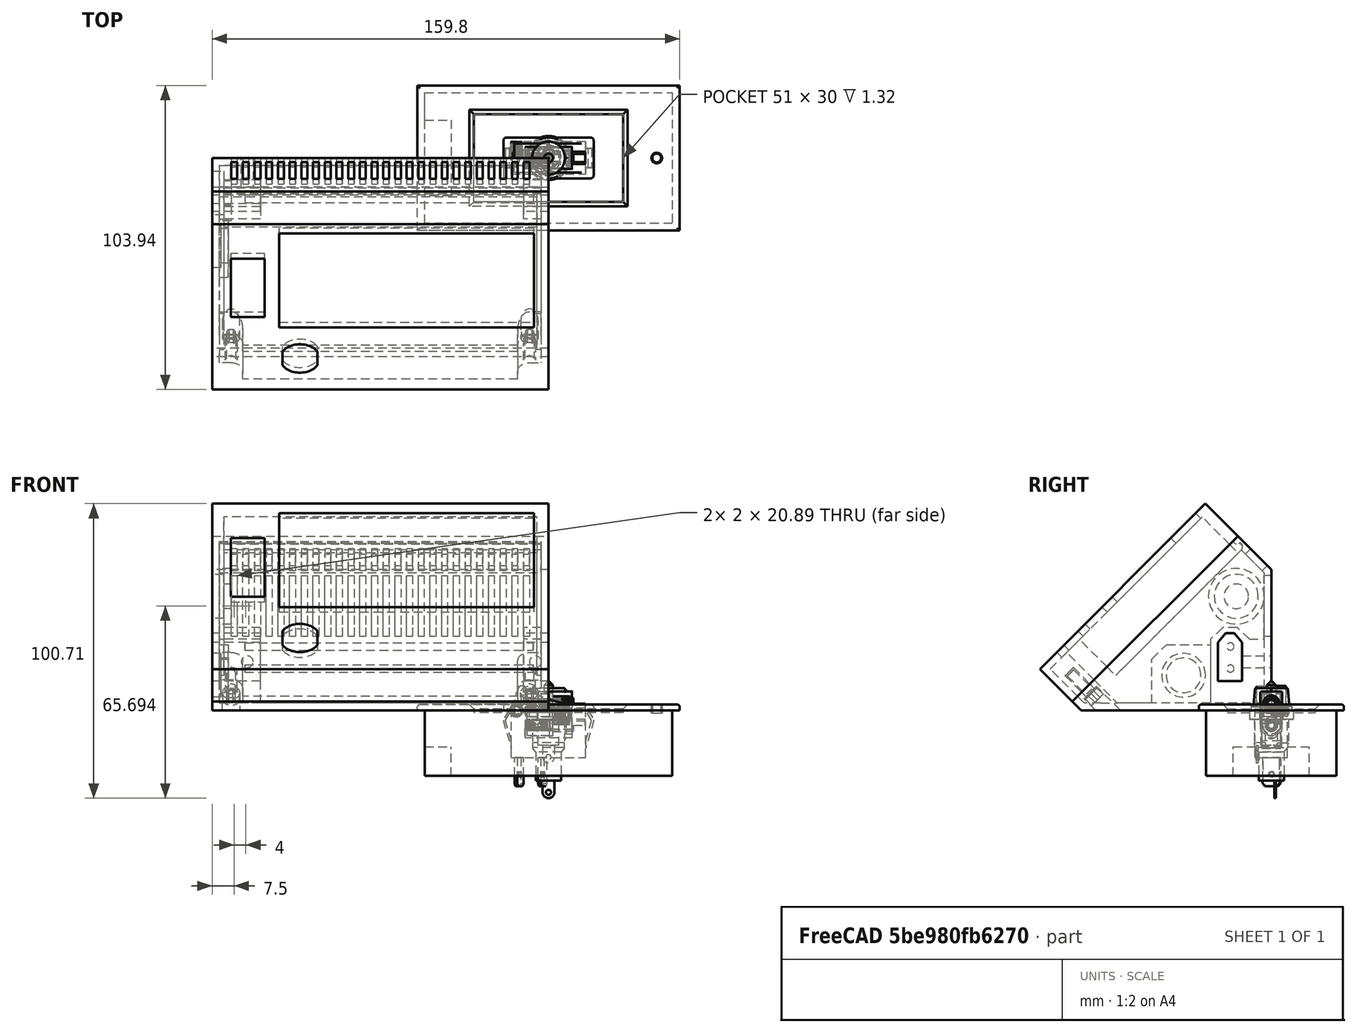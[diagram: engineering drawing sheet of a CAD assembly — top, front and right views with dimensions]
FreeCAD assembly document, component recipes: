
FREECAD ASSEMBLY — COMPONENT RECIPES ("moduleUI_017_Sur_base35mm_007.5")

This assembly document has 18 components, labeled P0..P17 below (a component is one placed body or linked part). 11 of them carry a construction recipe — the FreeCAD feature program that regenerates the part from scratch, quoted from this document or its linked companion documents; the rest are supplied as boundary geometry only. No exploded tour is included for this assembly.
COMPONENT P0 — recipe-attached ("base", modeled in this document).
Construction recipe (the document's own serialized feature program — sketch geometry with constraints, then the solid features built on it; lengths are millimeters unless a unit is written):

FEATURE [PartDesign::FeatureBase] Clone
  BaseFeature = -> Slice_child0
FEATURE [PartDesign::Thickness] Thickness
  Base = -> Clone [Face7]
  BaseFeature = -> Clone
  Intersection = false
  Join = 0
  Mode = 0
  Reversed = true
  SupportTransform = false
  Value = 2.5
  expr: Value = <<sp>>.epaisseurParois
FEATURE [PartDesign::Plane] DatumPlane001  label="planXt"
  AttachmentOffset = pos=(0,0,-2.5) rot=(0,0,1;0rad)
  Length = 110.737
  MapMode = 5
  Placement = pos=(-2.5,6e-16,-6e-16) rot=(0.57735,0.57735,0.57735;2.0944rad)
  ResizeMode = 0
  Support = -> [YZ_Plane002]
  Width = 102.305
  expr: .AttachmentOffset.Base.z = -<<sp>>.epaisseurParois
FEATURE [Sketcher::SketchObject] Sketch002  label="sk_renfortXt"
  FullyConstrained = true
  MapMode = 5
  Placement = pos=(-2.5,6e-16,-6e-16) rot=(0.57735,0.57735,0.57735;2.0944rad)
  Support = -> [DatumPlane001]
  expr: .Constraints.dist = <<sp>>.xt60distanceAngleBord
  expr: .Constraints.epRf = <<sp>>.xt60epRenfort
  expr: Constraints[13] = <<sp>>.xt60largeurFetiere
  expr: Constraints[14] = <<sp>>.xt60hauteur
  expr: Constraints[15] = <<sp>>.xt60hauteurToit
  expr: Constraints[16] = <<sp>>.xt60base
  expr: Constraints[18] = .Constraints.dist
  expr: Constraints[31] = <<sp>>.epaisseurParois
  expr: Constraints[32] = .Constraints.epRf
  expr: Constraints[34] = .Constraints.epRf
  expr: Constraints[45] = <<sp>>.epaisseurParois
  sketch-geometry (17):
    g0: LineSegment StartX=-18.3 StartY=10 StartZ=0 EndX=-18.3 EndY=23.25 EndZ=0
    g1: LineSegment StartX=-18.3 StartY=23.25 StartZ=0 EndX=-15.65 EndY=25.75 EndZ=0
    g2: LineSegment StartX=-15.65 StartY=25.75 StartZ=0 EndX=-12.65 EndY=25.75 EndZ=0
    g3: LineSegment StartX=-12.65 StartY=25.75 StartZ=0 EndX=-10 EndY=23.25 EndZ=0
    g4: LineSegment StartX=-10 StartY=23.25 StartZ=0 EndX=-10 EndY=10 EndZ=0
    g5: LineSegment StartX=-10 StartY=10 StartZ=0 EndX=-18.3 EndY=10 EndZ=0
    g6: LineSegment StartX=-14.15 StartY=10 StartZ=0 EndX=-14.15 EndY=25.75 EndZ=0
    g7: LineSegment StartX=-16.6431 StartY=28.25 StartZ=0 EndX=-20.8 EndY=24.3284 EndZ=0
    g8: LineSegment StartX=-20.8 StartY=24.3284 StartZ=0 EndX=-20.8 EndY=2.5 EndZ=0
    g9: LineSegment StartX=-20.8 StartY=2.5 StartZ=0 EndX=-7.5 EndY=2.5 EndZ=0
    g10: LineSegment StartX=-7.5 StartY=2.5 StartZ=0 EndX=-7.5 EndY=24.3284 EndZ=0
    g11: LineSegment StartX=-7.5 StartY=24.3284 StartZ=0 EndX=-11.6569 EndY=28.25 EndZ=0
    g12: LineSegment StartX=-11.6569 StartY=28.25 StartZ=0 EndX=-16.6431 EndY=28.25 EndZ=0
    g13: LineSegment StartX=-7.5 StartY=24.3284 StartZ=0 EndX=-2.5 EndY=24.3284 EndZ=0
    g14: LineSegment StartX=-2.5 StartY=24.3284 StartZ=0 EndX=-2.5 EndY=2.5 EndZ=0
    g15: LineSegment StartX=-2.5 StartY=2.5 StartZ=0 EndX=-7.5 EndY=2.5 EndZ=0
    g16: LineSegment StartX=-7.5 StartY=2.5 StartZ=0 EndX=-7.5 EndY=24.3284 EndZ=0
  constraints (46):
    c: Vertical(g0)
    c: Coincident(g0,g1)
    c: Coincident(g1,g2)
    c: Horizontal(g2)
    c: Coincident(g2,g3)
    c: Coincident(g3,g4)
    c: Vertical(g4)
    c: Coincident(g4,g5)
    c: Coincident(g5,g0)
    c: Horizontal(g5)
    c: Symmetric(g1,g2,g6)
    c: Equal(g0,g4)
    c: Symmetric(g0,g4,g6)
    c: DistanceX(g2,g2) = 3
    c: DistanceY(g4,g4) = 13.25
    c: DistanceY(g3,g2) = 2.5
    c: DistanceX(g5,g5) = 8.3
    c: DistanceX(g4,g-1) = 10  'dist'
    c: DistanceY(g-1,g4) = 10
    c: Coincident(g7,g8)
    c: Vertical(g8)
    c: Coincident(g8,g9)
    c: Horizontal(g9)
    c: Coincident(g9,g10)
    c: Coincident(g10,g11)
    c: Coincident(g11,g12)
    c: Coincident(g12,g7)
    c: Symmetric(g7,g10,g6)
    c: Symmetric(g7,g11,g6)
    c: Symmetric(g8,g9,g6)
    c: DistanceX(g8,g0) = 2.5  'epRf'
    c: DistanceY(g-1,g9) = 2.5
    c: Distance(g7,g1) = 2.5
    c: Parallel(g1,g7)
    c: DistanceY(g2,g11) = 2.5
    c: Coincident(g13,g14)
    c: Coincident(g14,g15)
    c: Coincident(g15,g16)
    c: Coincident(g16,g13)
    c: Horizontal(g13)
    c: Horizontal(g15)
    c: Vertical(g14)
    c: Vertical(g16)
    c: Coincident(g13,g11)
    c: Horizontal(g14,g9)
    c: DistanceX(g14,g-1) = 2.5
FEATURE [PartDesign::Pad] Pad001  label="renfortXt"
  AllowMultiFace = false
  BaseFeature = -> Thickness
  Direction = (1,-1e-16,1e-16)
  Length = 110
  Length2 = 100
  Profile = -> Sketch002
  Reversed = true
  Type = 0
  expr: Length = <<sp>>.largeurModuleBase - 2 * <<sp>>.epaisseurParois
FEATURE [Sketcher::SketchObject] Sketch003  label="sk_trouXt"
  FullyConstrained = true
  MapMode = 5
  Placement = pos=(0,0,0) rot=(0.57735,0.57735,0.57735;2.0944rad)
  Support = -> [YZ_Plane002]
  expr: .Constraints.dist = <<sp>>.xt60distanceAngleBord
  expr: Constraints[13] = <<sp>>.xt60base
  expr: Constraints[14] = <<sp>>.xt60hauteur
  expr: Constraints[15] = <<sp>>.xt60hauteurToit + <<sp>>.xtJeu
  expr: Constraints[16] = <<sp>>.xt60largeurFetiere
  expr: Constraints[18] = .Constraints.dist
  sketch-geometry (7):
    g0: LineSegment StartX=-18.3 StartY=10 StartZ=0 EndX=-18.3 EndY=23.25 EndZ=0
    g1: LineSegment StartX=-18.3 StartY=23.25 StartZ=0 EndX=-15.65 EndY=26.35 EndZ=0
    g2: LineSegment StartX=-15.65 StartY=26.35 StartZ=0 EndX=-12.65 EndY=26.35 EndZ=0
    g3: LineSegment StartX=-12.65 StartY=26.35 StartZ=0 EndX=-10 EndY=23.25 EndZ=0
    g4: LineSegment StartX=-10 StartY=23.25 StartZ=0 EndX=-10 EndY=10 EndZ=0
    g5: LineSegment StartX=-10 StartY=10 StartZ=0 EndX=-18.3 EndY=10 EndZ=0
    g6: LineSegment StartX=-14.15 StartY=10 StartZ=0 EndX=-14.15 EndY=26.35 EndZ=0
  constraints (19):
    c: Vertical(g0)
    c: Coincident(g0,g1)
    c: Coincident(g1,g2)
    c: Horizontal(g2)
    c: Coincident(g2,g3)
    c: Coincident(g3,g4)
    c: Coincident(g4,g5)
    c: Coincident(g5,g0)
    c: Horizontal(g5)
    c: Symmetric(g1,g2,g6)
    c: Symmetric(g0,g3,g6)
    c: Vertical(g6)
    c: Symmetric(g0,g4,g6)
    c: DistanceX(g5,g5) = 8.3
    c: DistanceY(g4,g4) = 13.25
    c: DistanceY(g3,g2) = 3.1
    c: DistanceX(g2,g2) = 3
    c: DistanceX(g4,g-1) = 10  'dist'
    c: DistanceY(g-1,g4) = 10
FEATURE [PartDesign::Pocket] Pocket
  AllowMultiFace = false
  BaseFeature = -> Pad001
  Direction = (-1,2e-16,-3e-16)
  Length = 115
  Length2 = 100
  Profile = -> Sketch003
  Type = 0
  expr: Length = <<sp>>.largeurModuleBase
FEATURE [PartDesign::Plane] DatumPlane002  label="planDecoupeRenfortXt"
  AttachmentOffset = pos=(0,0,2.5) rot=(0,0,1;0rad)
  Length = 161.762
  MapMode = 5
  Placement = pos=(0,-2.5,-6e-16) rot=(1,0,0;1.5708rad)
  ResizeMode = 0
  Support = -> [XZ_Plane002]
  Width = 106.331
  expr: .AttachmentOffset.Base.z = <<sp>>.epaisseurParois
FEATURE [Sketcher::SketchObject] Sketch004  label="sk_decoupRenfXt"
  FullyConstrained = true
  MapMode = 5
  Placement = pos=(0,-2.5,-6e-16) rot=(1,0,0;1.5708rad)
  Support = -> [DatumPlane002]
  expr: Constraints[10] = <<sp>>.xt60LongueurRenfortPetit + <<sp>>.epaisseurParois
  expr: Constraints[11] = <<sp>>.largeurModuleBase - (<<sp>>.xt60longueurRenfortGrand + <<sp>>.epaisseurParois)
  expr: Constraints[8] = <<sp>>.epaisseurParois
  expr: Constraints[9] = <<sp>>.xt60distanceAngleBord + <<sp>>.xt60hauteur + <<sp>>.xt60hauteurToit + <<sp>>.xt60epRenfort
  sketch-geometry (4):
    g0: LineSegment StartX=-98.5 StartY=28.25 StartZ=0 EndX=-8.5 EndY=28.25 EndZ=0
    g1: LineSegment StartX=-8.5 StartY=28.25 StartZ=0 EndX=-8.5 EndY=2.5 EndZ=0
    g2: LineSegment StartX=-8.5 StartY=2.5 StartZ=0 EndX=-98.5 EndY=2.5 EndZ=0
    g3: LineSegment StartX=-98.5 StartY=2.5 StartZ=0 EndX=-98.5 EndY=28.25 EndZ=0
  constraints (12):
    c: Coincident(g0,g1)
    c: Coincident(g1,g2)
    c: Coincident(g2,g3)
    c: Coincident(g3,g0)
    c: Horizontal(g0)
    c: Horizontal(g2)
    c: Vertical(g1)
    c: Vertical(g3)
    c: DistanceY(g-1,g1) = 2.5
    c: DistanceY(g-1,g0) = 28.25
    c: DistanceX(g1,g-1) = 8.5
    c: DistanceX(g2,g-1) = 98.5
FEATURE [PartDesign::Pocket] Pocket001  label="decoupeRenfXt"
  AllowMultiFace = false
  BaseFeature = -> Pocket
  Direction = (0,1,2e-16)
  Length = 23.3
  Length2 = 100
  Profile = -> Sketch004
  Reversed = true
  Type = 0
  expr: Length = <<sp>>.xt60distanceAngleBord + <<sp>>.xt60base + 2 * <<sp>>.xt60epRenfort
FEATURE [Sketcher::SketchObject] Sketch005  label="xt60PercagePostMale"
  FullyConstrained = true
  MapMode = 5
  Placement = pos=(0,0,0) rot=(1,0,0;1.5708rad)
  Support = -> [XZ_Plane002]
  expr: Constraints[0] = <<sp>>.insertDiamPercage
  expr: Constraints[1] = <<sp>>.insertDistanceTrouBordMale
  expr: Constraints[2] = <<sp>>.insertHauteur
  sketch-geometry (1):
    g0: Circle CenterX=-4.5 CenterY=16.625 CenterZ=0 NormalX=0 NormalY=0 NormalZ=1 AngleXU=0 Radius=2
  constraints (3):
    c: Diameter(g0) = 4
    c: DistanceX(g0,g-1) = 4.5
    c: DistanceY(g-1,g0) = 16.625
FEATURE [PartDesign::Pocket] Pocket002  label="insertXtMale"
  AllowMultiFace = false
  BaseFeature = -> Pocket001
  Direction = (0,1,2e-16)
  Length = 10
  Length2 = 100
  Profile = -> Sketch005
  Reversed = true
  Type = 0
  expr: Length = <<sp>>.insertProfondeurPercage
FEATURE [Sketcher::SketchObject] Sketch006  label="xt60PercagePostFem"
  FullyConstrained = true
  MapMode = 5
  Placement = pos=(0,0,0) rot=(1,0,0;1.5708rad)
  Support = -> [XZ_Plane002]
  expr: Constraints[0] = <<sp>>.insertDiamPercage
  expr: Constraints[1] = <<sp>>.insertDistanceTrouBordFem
  expr: Constraints[2] = <<sp>>.insertHauteur
  sketch-geometry (1):
    g0: Circle CenterX=-103 CenterY=16.625 CenterZ=0 NormalX=0 NormalY=0 NormalZ=1 AngleXU=0 Radius=2
  constraints (3):
    c: Diameter(g0) = 4
    c: DistanceX(g0,g-1) = 103
    c: DistanceY(g-1,g0) = 16.625
FEATURE [PartDesign::Pocket] Pocket003  label="insertXt60Fem"
  AllowMultiFace = false
  BaseFeature = -> Pocket002
  Direction = (0,1,2e-16)
  Length = 10
  Length2 = 100
  Profile = -> Sketch006
  Reversed = true
  Type = 0
  expr: Length = <<sp>>.insertProfondeurPercage
FEATURE [PartDesign::Plane] DatumPlane003
  AttachmentOffset = pos=(0,0,2.5) rot=(0,0,1;0rad)
  Length = 162.821
  MapMode = 2
  Placement = pos=(0,0,2.5) rot=(0,0,1;0rad)
  ResizeMode = 0
  Support = -> [XY_Plane002]
  Width = 115.821
  expr: .AttachmentOffset.Base.z = <<sp>>.epaisseurParois
FEATURE [PartDesign::Plane] DatumPlane004  label="planTrancheur"
  AttachmentOffset = pos=(0,0,71) rot=(-1,0,0;0.785398rad)
  Length = 166.517
  MapMode = 5
  Placement = pos=(0,-71,-1.58e-14) rot=(1,0,0;0.785398rad)
  ResizeMode = 0
  Support = -> [XZ_Plane002]
  Width = 152.077
  expr: .AttachmentOffset.Base.z = <<sp>>.planTrancheur
FEATURE [Sketcher::SketchObject] Sketch008
  FullyConstrained = true
  MapMode = 5
  Placement = pos=(0,-71,-2.13e-14) rot=(1,0,0;0.785398rad)
  Support = -> [DatumPlane004]
  expr: .Constraints.dist = <<sp>>.epaisseurParois
  expr: Constraints[13] = <<sp>>.epaisseurParois
  expr: Constraints[16] = <<sp>>.insertDiamPercage / 2 + <<sp>>.insertFAVMargeDist
  expr: Constraints[1] = <<sp>>.insertFavDistAuZeroDuPLan
  expr: Constraints[21] = <<sp>>.insertFAVDistBord
  expr: Constraints[22] = <<sp>>.largeurModuleBase - <<sp>>.epaisseurParois
  sketch-geometry (7):
    g0: LineSegment StartX=-2.5 StartY=4.24264 StartZ=0 EndX=-112.5 EndY=4.24264 EndZ=0
    g1: LineSegment StartX=-6.5 StartY=14.7426 StartZ=0 EndX=-2.5 EndY=14.7426 EndZ=0
    g2: LineSegment StartX=-2.5 StartY=14.7426 StartZ=0 EndX=-2.5 EndY=6.74264 EndZ=0
    g3: LineSegment StartX=-2.5 StartY=6.74264 StartZ=0 EndX=-10.5 EndY=6.74264 EndZ=0
    g4: LineSegment StartX=-10.5 StartY=6.74264 StartZ=0 EndX=-10.5 EndY=10.7426 EndZ=0
    g5: ArcOfCircle CenterX=-6.5 CenterY=10.7426 CenterZ=0 NormalX=0 NormalY=0 NormalZ=1 AngleXU=0 Radius=4 StartAngle=1.5708 EndAngle=3.14159
    g6: LineSegment StartX=-6.5 StartY=10.7426 StartZ=0 EndX=-6.5 EndY=6.74264 EndZ=0
  constraints (23):
    c: Horizontal(g0)
    c: DistanceY(g-1,g0) = 4.24264
    c: DistanceX(g0,g-1) = 2.5  'dist'
    c: Horizontal(g1)
    c: Coincident(g1,g2)
    c: Vertical(g2)
    c: Coincident(g2,g3)
    c: Horizontal(g3)
    c: Coincident(g3,g4)
    c: Vertical(g4)
    c: Vertical(g2,g0)
    c: Equal(g3,g2)
    c: Equal(g4,g1)
    c: DistanceY(g0,g2) = 2.5
    c: Coincident(g5,g4)
    c: Coincident(g5,g1)
    c: DistanceX(g5,g2) = 4
    c: Coincident(g6,g5)
    c: PointOnObject(g6,g3)
    c: Vertical(g6)
    c: Vertical(g5,g1)
    c: DistanceX(g3,g3) = 8
    c: DistanceX(g0,g-1) = 112.5
FEATURE [PartDesign::Pad] Pad003  label="padTrouFAVDroite"
  AllowMultiFace = false
  BaseFeature = -> Pocket003
  Direction = (0,-0.707107,0.707107)
  Length = 10
  Length2 = 100
  Profile = -> Sketch008
  Reversed = true
  Type = 3
  UpToFace = -> DatumPlane003
FEATURE [Sketcher::SketchObject] Sketch009
  FullyConstrained = true
  MapMode = 5
  Placement = pos=(0,-71,-2.13e-14) rot=(1,0,0;0.785398rad)
  Support = -> [DatumPlane004]
  expr: .Constraints.larg = <<sp>>.insertFAVDistBord
  expr: Constraints[11] = .Constraints.larg / 2
  expr: Constraints[12] = <<sp>>.largeurModuleBase
  expr: Constraints[13] = <<sp>>.insertFavDistAuZeroDuPLan
  expr: Constraints[14] = <<sp>>.epaisseurParois
  expr: Constraints[15] = <<sp>>.epaisseurParois
  expr: Constraints[8] = .Constraints.larg
  sketch-geometry (6):
    g0: LineSegment StartX=-112.5 StartY=6.74264 StartZ=0 EndX=-104.5 EndY=6.74264 EndZ=0
    g1: LineSegment StartX=-104.5 StartY=6.74264 StartZ=0 EndX=-104.5 EndY=10.7426 EndZ=0
    g2: LineSegment StartX=-108.5 StartY=14.7426 StartZ=0 EndX=-112.5 EndY=14.7426 EndZ=0
    g3: LineSegment StartX=-112.5 StartY=14.7426 StartZ=0 EndX=-112.5 EndY=6.74264 EndZ=0
    g4: ArcOfCircle CenterX=-108.5 CenterY=10.7426 CenterZ=0 NormalX=0 NormalY=0 NormalZ=1 AngleXU=0 Radius=4 StartAngle=0 EndAngle=1.5708
    g5: GeomPoint X=-115 Y=4.24264 Z=0
  constraints (16):
    c: Coincident(g0,g1)
    c: Coincident(g2,g3)
    c: Coincident(g3,g0)
    c: Horizontal(g0)
    c: Horizontal(g2)
    c: Vertical(g1)
    c: Vertical(g3)
    c: DistanceX(g0,g0) = 8  'larg'
    c: DistanceY(g3,g3) = 8
    c: Tangent(g2,g4) = -1.5708
    c: Tangent(g1,g4) = -1.5708
    c: DistanceX(g0,g4) = 4
    c: DistanceX(g5,g-1) = 115
    c: DistanceY(g-1,g5) = 4.24264
    c: DistanceX(g5,g0) = 2.5
    c: DistanceY(g5,g0) = 2.5
FEATURE [PartDesign::Pad] Pad004  label="padTrouFavGauche"
  AllowMultiFace = false
  BaseFeature = -> Pad003
  Direction = (0,-0.707107,0.707107)
  Length = 10
  Length2 = 100
  Profile = -> Sketch009
  Type = 3
  UpToFace = -> DatumPlane003 [Plane]
FEATURE [Sketcher::SketchObject] Sketch010
  FullyConstrained = true
  MapMode = 5
  Placement = pos=(0,-71,-2.13e-14) rot=(1,0,0;0.785398rad)
  Support = -> [DatumPlane004]
  expr: Constraints[0] = <<sp>>.insertFAVDistBord / 2 + <<sp>>.epaisseurParois
  expr: Constraints[1] = <<sp>>.insertFavDistAuZeroDuPLan + <<sp>>.epaisseurParois + <<sp>>.insertFAVDistBord / 2
  expr: Constraints[2] = <<sp>>.insertDiamPercage
  sketch-geometry (1):
    g0: Circle CenterX=-6.5 CenterY=10.7426 CenterZ=0 NormalX=0 NormalY=0 NormalZ=1 AngleXU=0 Radius=2
  constraints (3):
    c: DistanceX(g0,g-1) = 6.5
    c: DistanceY(g-1,g0) = 10.7426
    c: Diameter(g0) = 4
FEATURE [PartDesign::Pocket] Pocket004  label="trouDroit"
  AllowMultiFace = false
  BaseFeature = -> Pad004
  Direction = (0,0.707107,-0.707107)
  Length = 5
  Length2 = 100
  Profile = -> Sketch010
  Type = 1
FEATURE [Sketcher::SketchObject] Sketch011
  FullyConstrained = true
  MapMode = 5
  Placement = pos=(0,-71,-2.13e-14) rot=(1,0,0;0.785398rad)
  Support = -> [DatumPlane004]
  expr: Constraints[0] = <<sp>>.insertDiamPercage
  expr: Constraints[1] = <<sp>>.largeurModuleBase - <<sp>>.epaisseurParois - <<sp>>.insertFAVDistBord / 2
  expr: Constraints[2] = <<sp>>.insertFavDistAuZeroDuPLan + <<sp>>.epaisseurParois + <<sp>>.insertFAVDistBord / 2
  sketch-geometry (1):
    g0: Circle CenterX=-108.5 CenterY=10.7426 CenterZ=0 NormalX=0 NormalY=0 NormalZ=1 AngleXU=0 Radius=2
  constraints (3):
    c: Diameter(g0) = 4
    c: DistanceX(g0,g-1) = 108.5
    c: DistanceY(g-1,g0) = 10.7426
FEATURE [PartDesign::Pocket] Pocket005  label="trouGauche"
  AllowMultiFace = false
  BaseFeature = -> Pocket004
  Direction = (0,0.707107,-0.707107)
  Length = 5
  Length2 = 100
  Profile = -> Sketch011
  Type = 1
FEATURE [PartDesign::Plane] DatumPlane005  label="planTeteVisFav"
  AttachmentOffset = pos=(0,0,68) rot=(-1,0,0;0.785398rad)
  Length = 166.517
  MapMode = 5
  Placement = pos=(0,-68,-1.51e-14) rot=(1,0,0;0.785398rad)
  ResizeMode = 0
  Support = -> [XZ_Plane002]
  Width = 152.077
  expr: .AttachmentOffset.Base.z = <<sp>>.planTrancheur - 3
FEATURE [Sketcher::SketchObject] Sketch012
  ExternalGeometry = -> [Pocket005]
  FullyConstrained = true
  MapMode = 5
  Placement = pos=(0,-68,-1.42e-14) rot=(1,0,0;0.785398rad)
  Support = -> [DatumPlane005]
  expr: Constraints[1] = <<sp>>.visM3DiamEncastrement
  sketch-geometry (2):
    g0: Circle CenterX=-6.5 CenterY=8.62132 CenterZ=0 NormalX=0 NormalY=0 NormalZ=1 AngleXU=0 Radius=3
    g1: Circle CenterX=-108.5 CenterY=8.62132 CenterZ=0 NormalX=0 NormalY=0 NormalZ=1 AngleXU=0 Radius=3
  constraints (4):
    c: Equal(g0,g1)
    c: Diameter(g1) = 6
    c: Coincident(g1,g-4)
    c: Coincident(g-3,g0)
FEATURE [PartDesign::Pocket] Pocket006  label="evidementTeteVisFav"
  AllowMultiFace = false
  BaseFeature = -> Pocket005
  Direction = (0,0.707107,-0.707107)
  Length = 20
  Length2 = 100
  Profile = -> Sketch012
  Type = 1
FEATURE [Sketcher::SketchObject] Sketch014
  FullyConstrained = true
  MapMode = 5
  Placement = pos=(0,0,0) rot=(1,0,0;1.5708rad)
  Support = -> [XZ_Plane002]
  expr: Constraints[12] = <<sp>>.xt60distanceAngleBord + <<sp>>.xt60hauteur + <<sp>>.ventilDistBordFente
  expr: Constraints[13] = <<sp>>.ventilLargeurFentes
  expr: Constraints[14] = <<sp>>.ventilEcartfente / 2
  expr: Constraints[15] = <<sp>>.hauteurDuDos - <<sp>>.ventilDistBordFente
  expr: Constraints[2] = <<sp>>.hauteurDuDos
  expr: Constraints[3] = <<sp>>.largeurModuleBase / 2
  sketch-geometry (5):
    g0: LineSegment StartX=-57.5 StartY=0 StartZ=0 EndX=-57.5 EndY=48.1371 EndZ=0
    g1: LineSegment StartX=-60.5 StartY=46.1371 StartZ=0 EndX=-58.5 EndY=46.1371 EndZ=0
    g2: LineSegment StartX=-58.5 StartY=46.1371 StartZ=0 EndX=-58.5 EndY=25.25 EndZ=0
    g3: LineSegment StartX=-58.5 StartY=25.25 StartZ=0 EndX=-60.5 EndY=25.25 EndZ=0
    g4: LineSegment StartX=-60.5 StartY=25.25 StartZ=0 EndX=-60.5 EndY=46.1371 EndZ=0
  constraints (16):
    c: PointOnObject(g0,g-1)
    c: Vertical(g0)
    c: DistanceY(g0,g0) = 48.1371
    c: DistanceX(g0,g-1) = 57.5
    c: Coincident(g1,g2)
    c: Coincident(g2,g3)
    c: Coincident(g3,g4)
    c: Coincident(g4,g1)
    c: Horizontal(g1)
    c: Horizontal(g3)
    c: Vertical(g2)
    c: Vertical(g4)
    c: DistanceY(g-1,g2) = 25.25
    c: DistanceX(g1,g1) = 2
    c: DistanceX(g2,g0) = 1
    c: DistanceY(g-1,g1) = 46.1371
FEATURE [PartDesign::Pocket] Pocket008  label="ventilFente1"
  AllowMultiFace = false
  BaseFeature = -> Pocket006
  Direction = (0,1,2e-16)
  Length = 2.5
  Length2 = 100
  Profile = -> Sketch014
  Reversed = true
  Type = 0
  expr: Length = <<sp>>.epaisseurParois
FEATURE [PartDesign::LinearPattern] LinearPattern  label="ventilDosRepeat1"
  BaseFeature = -> Pocket008
  Direction = -> Sketch014 [H_Axis]
  Length = 48
  Occurrences = 13
  Originals = -> [Pocket008]
  Reversed = true
  expr: Length = <<sp>>.ventilLargeurRepet
  expr: Occurrences = <<sp>>.ventilNbrFents
FEATURE [PartDesign::LinearPattern] LinearPattern001  label="ventilDosRepeat2"
  BaseFeature = -> LinearPattern
  Direction = -> Sketch014 [H_Axis]
  Length = 52
  Occurrences = 14
  Originals = -> [Pocket008]
  expr: Length = <<sp>>.ventilLargeurRepet + <<sp>>.ventilEcartfente + <<sp>>.ventilLargeurFentes
  expr: Occurrences = <<sp>>.ventilNbrFents + 1
FEATURE [PartDesign::Plane] DatumPlane006  label="planVentilSup"
  AttachmentOffset = pos=(0,0,-48.1371) rot=(1,0,0;0.785398rad)
  Length = 166.517
  MapMode = 5
  Placement = pos=(0,48.1371,1.07e-14) rot=(1,0,0;2.35619rad)
  ResizeMode = 0
  Support = -> [XZ_Plane002]
  Width = 152.077
  expr: .AttachmentOffset.Base.z = -<<sp>>.hauteurDuDos
FEATURE [Sketcher::SketchObject] Sketch015
  FullyConstrained = true
  MapMode = 5
  Placement = pos=(0,48.1371,1.07e-14) rot=(1,0,0;2.35619rad)
  Support = -> [DatumPlane006]
  expr: Constraints[10] = <<sp>>.ventilLargeurFentes
  expr: Constraints[11] = (<<sp>>.largeurModuleBase + <<sp>>.ventilEcartfente) / 2
  expr: Constraints[8] = <<sp>>.distanceAuZeroPlanBorArriere + <<sp>>.ventilDistBordFente
  expr: Constraints[9] = <<sp>>.longPetitRetSupSansFav - 2 * <<sp>>.ventilDistBordFente - <<sp>>.favBordureProf
  sketch-geometry (4):
    g0: LineSegment StartX=-58.5 StartY=78.0926 StartZ=0 EndX=-60.5 EndY=78.0926 EndZ=0
    g1: LineSegment StartX=-60.5 StartY=78.0926 StartZ=0 EndX=-60.5 EndY=70.0761 EndZ=0
    g2: LineSegment StartX=-60.5 StartY=70.0761 StartZ=0 EndX=-58.5 EndY=70.0761 EndZ=0
    g3: LineSegment StartX=-58.5 StartY=70.0761 StartZ=0 EndX=-58.5 EndY=78.0926 EndZ=0
  constraints (12):
    c: Coincident(g0,g1)
    c: Coincident(g1,g2)
    c: Coincident(g2,g3)
    c: Coincident(g3,g0)
    c: Horizontal(g0)
    c: Horizontal(g2)
    c: Vertical(g1)
    c: Vertical(g3)
    c: DistanceY(g-1,g2) = 70.0761
    c: DistanceY(g2,g0) = 8.01652
    c: DistanceX(g0,g0) = 2
    c: DistanceX(g2,g-1) = 58.5
FEATURE [PartDesign::Pocket] Pocket009  label="ventilSupFente"
  AllowMultiFace = false
  BaseFeature = -> LinearPattern001
  Direction = (0,0.707107,0.707107)
  Length = 5
  Length2 = 100
  Profile = -> Sketch015
  Reversed = true
  Type = 0
FEATURE [PartDesign::LinearPattern] LinearPattern002  label="ventilSupRepeat1"
  BaseFeature = -> Pocket009
  Direction = -> Sketch015 [H_Axis]
  Length = 48
  Occurrences = 13
  Originals = -> [Pocket009]
  Reversed = true
  expr: Length = <<sp>>.ventilLargeurRepet
  expr: Occurrences = <<sp>>.ventilNbrFents
FEATURE [PartDesign::LinearPattern] LinearPattern003  label="ventilSupRepeat2"
  BaseFeature = -> LinearPattern002
  Direction = -> Sketch015 [H_Axis]
  Length = 52
  Occurrences = 14
  Originals = -> [Pocket009]
  expr: Length = <<sp>>.ventilLargeurRepet + <<sp>>.ventilEcartfente + <<sp>>.ventilLargeurFentes
  expr: Occurrences = <<sp>>.ventilNbrFents + 1
FEATURE [PartDesign::Body] Body001  label="base"
  BaseFeature = -> Slice_child0
  Group = -> [Clone,Thickness,DatumPlane001,Sketch002,Pad001,Sketch003,Pocket,DatumPlane002,Sketch004,Pocket001,Sketch005,Pocket002,Sketch006,Pocket003,DatumPlane003,DatumPlane004,Sketch008,Pad003,Sketch009,Pad004,Sketch010,Pocket004,Sketch011,Pocket005,DatumPlane005,Sketch012,Pocket006,Sketch014,Pocket008,LinearPattern,LinearPattern001,DatumPlane006,Sketch015,Pocket009,LinearPattern002,LinearPattern003,+15 more]
  Origin = -> Origin002
  Tip = -> Pocket029
COMPONENT P1 — recipe-attached ("faceAvant", modeled in this document).
Construction recipe (the document's own serialized feature program — sketch geometry with constraints, then the solid features built on it; lengths are millimeters unless a unit is written):

FEATURE [PartDesign::FeatureBase] Clone001
  BaseFeature = -> Slice_child1
FEATURE [PartDesign::Thickness] Thickness001
  Base = -> Clone001 [Face5]
  BaseFeature = -> Clone001
  Intersection = false
  Join = 0
  Mode = 0
  Reversed = true
  SupportTransform = false
  Value = 2.5
  expr: Value = <<sp>>.epaisseurParois
FEATURE [PartDesign::Plane] DatumPlane007  label="planTrancheurBis"
  AttachmentOffset = pos=(0,0,71) rot=(-1,0,0;0.785398rad)
  Length = 168.131
  MapMode = 5
  Placement = pos=(0,-71,-1.58e-14) rot=(1,0,0;0.785398rad)
  ResizeMode = 0
  Support = -> [XZ_Plane003]
  Width = 169.449
  expr: .AttachmentOffset.Base.z = <<sp>>.planTrancheur
FEATURE [Sketcher::SketchObject] Sketch016  label="sk_insertFavDroit"
  FullyConstrained = true
  MapMode = 5
  Placement = pos=(0,-71,-2.13e-14) rot=(1,0,0;0.785398rad)
  Support = -> [DatumPlane007]
  expr: Constraints[11] = <<sp>>.insertFAVDistBord
  expr: Constraints[14] = <<sp>>.insertFAVDistBord / 2
  expr: Constraints[7] = <<sp>>.epaisseurParois
  expr: Constraints[8] = <<sp>>.insertFavDistAuZeroDuPLan + <<sp>>.epaisseurParois
  expr: Constraints[9] = <<sp>>.insertFAVDistBord
  sketch-geometry (5):
    g0: LineSegment StartX=-6.5 StartY=14.7426 StartZ=0 EndX=-2.5 EndY=14.7426 EndZ=0
    g1: LineSegment StartX=-2.5 StartY=14.7426 StartZ=0 EndX=-2.5 EndY=6.74264 EndZ=0
    g2: LineSegment StartX=-2.5 StartY=6.74264 StartZ=0 EndX=-10.5 EndY=6.74264 EndZ=0
    g3: LineSegment StartX=-10.5 StartY=6.74264 StartZ=0 EndX=-10.5 EndY=10.7426 EndZ=0
    g4: ArcOfCircle CenterX=-6.5 CenterY=10.7426 CenterZ=0 NormalX=0 NormalY=0 NormalZ=1 AngleXU=0 Radius=4 StartAngle=1.5708 EndAngle=3.14159
  constraints (15):
    c: Horizontal(g0)
    c: Coincident(g0,g1)
    c: Vertical(g1)
    c: Coincident(g1,g2)
    c: Horizontal(g2)
    c: Coincident(g2,g3)
    c: Vertical(g3)
    c: DistanceX(g1,g-1) = 2.5
    c: DistanceY(g-1,g1) = 6.74264
    c: DistanceY(g1,g1) = 8
    c: Equal(g3,g0)
    c: DistanceX(g2,g2) = 8
    c: Coincident(g4,g0)
    c: Tangent(g4,g3) = 1.5708
    c: DistanceX(g4,g1) = 4
FEATURE [PartDesign::Pad] Pad005  label="padInsertFavDroit"
  AllowMultiFace = false
  BaseFeature = -> Thickness001
  Direction = (1,1,1)
  Length = 10
  Length2 = 100
  Profile = -> Sketch016
  Type = 2
FEATURE [Sketcher::SketchObject] Sketch017  label="sp_padInserFavGauch"
  FullyConstrained = true
  MapMode = 5
  Placement = pos=(0,-71,-2.13e-14) rot=(1,0,0;0.785398rad)
  Support = -> [DatumPlane007]
  expr: Constraints[10] = <<sp>>.insertFAVDistBord
  expr: Constraints[12] = <<sp>>.insertFAVDistBord / 2
  expr: Constraints[13] = <<sp>>.largeurModuleBase
  expr: Constraints[14] = <<sp>>.insertFavDistAuZeroDuPLan
  expr: Constraints[15] = <<sp>>.epaisseurParois
  expr: Constraints[16] = <<sp>>.epaisseurParois
  sketch-geometry (6):
    g0: LineSegment StartX=-108.5 StartY=14.7426 StartZ=0 EndX=-112.5 EndY=14.7426 EndZ=0
    g1: LineSegment StartX=-112.5 StartY=14.7426 StartZ=0 EndX=-112.5 EndY=6.74264 EndZ=0
    g2: LineSegment StartX=-112.5 StartY=6.74264 StartZ=0 EndX=-104.5 EndY=6.74264 EndZ=0
    g3: LineSegment StartX=-104.5 StartY=6.74264 StartZ=0 EndX=-104.5 EndY=10.7426 EndZ=0
    g4: ArcOfCircle CenterX=-108.5 CenterY=10.7426 CenterZ=0 NormalX=0 NormalY=0 NormalZ=1 AngleXU=0 Radius=4 StartAngle=2.3e-15 EndAngle=1.5708
    g5: GeomPoint X=-115 Y=4.24264 Z=0
  constraints (17):
    c: Horizontal(g0)
    c: Coincident(g0,g1)
    c: Vertical(g1)
    c: Coincident(g1,g2)
    c: Horizontal(g2)
    c: Coincident(g2,g3)
    c: Vertical(g3)
    c: Equal(g3,g0)
    c: Equal(g2,g1)
    c: Coincident(g0,g4)
    c: DistanceX(g2,g2) = 8
    c: Tangent(g4,g3) = -1.5708
    c: DistanceX(g0,g0) = 4
    c: DistanceX(g5,g-1) = 115
    c: DistanceY(g-1,g5) = 4.24264
    c: DistanceY(g5,g1) = 2.5
    c: DistanceX(g5,g1) = 2.5
FEATURE [PartDesign::Pad] Pad006  label="padInsertFavGauch"
  AllowMultiFace = false
  BaseFeature = -> Pad005
  Direction = (1,1,1)
  Length = 10
  Length2 = 100
  Profile = -> Sketch017
  Type = 2
FEATURE [Sketcher::SketchObject] Sketch018  label="skPercageInsertFavDroit"
  FullyConstrained = true
  MapMode = 5
  Placement = pos=(0,-71,-2.13e-14) rot=(1,0,0;0.785398rad)
  Support = -> [DatumPlane007]
  expr: Constraints[0] = <<sp>>.insertDiamPercage
  expr: Constraints[1] = <<sp>>.insertFavDistAuZeroDuPLan + <<sp>>.epaisseurParois + <<sp>>.insertFAVDistBord / 2
  expr: Constraints[2] = <<sp>>.epaisseurParois + <<sp>>.insertFAVDistBord / 2
  expr: Constraints[7] = <<sp>>.largeurModuleBase - 2 * <<sp>>.epaisseurParois - <<sp>>.insertFAVDistBord
  sketch-geometry (3):
    g0: Circle CenterX=-6.5 CenterY=10.7426 CenterZ=0 NormalX=0 NormalY=0 NormalZ=1 AngleXU=0 Radius=2
    g1: Circle CenterX=-108.5 CenterY=10.7426 CenterZ=0 NormalX=0 NormalY=0 NormalZ=1 AngleXU=0 Radius=2
    g2: LineSegment StartX=-108.5 StartY=10.7426 StartZ=0 EndX=-6.5 EndY=10.7426 EndZ=0
  constraints (8):
    c: Diameter(g0) = 4
    c: DistanceY(g-1,g0) = 10.7426
    c: DistanceX(g0,g-1) = 6.5
    c: Equal(g0,g1)
    c: Coincident(g2,g1)
    c: Coincident(g2,g0)
    c: Horizontal(g2)
    c: DistanceX(g2,g2) = 102
FEATURE [PartDesign::Pocket] Pocket010  label="trouInsertFavDroit"
  AllowMultiFace = false
  BaseFeature = -> Pad006
  Direction = (1,1,1)
  Length = 8
  Length2 = 100
  Profile = -> Sketch018
  Reversed = true
  Type = 0
  expr: Length = <<sp>>.insertFavProfondeur
FEATURE [PartDesign::Plane] DatumPlane011  label="planFaceAvant"
  AttachmentOffset = pos=(0,0,93.2843) rot=(-1,0,0;0.785398rad)
  Length = 168.131
  MapMode = 5
  Placement = pos=(0,-93.2843,-2.07e-14) rot=(1,0,0;0.785398rad)
  ResizeMode = 0
  Support = -> [XZ_Plane003]
  Width = 169.449
  expr: .AttachmentOffset.Base.z = <<sp>>.planFaceAvant
FEATURE [Sketcher::SketchObject] Sketch030  label="sk_rebordFav"
  FullyConstrained = true
  MapMode = 5
  Placement = pos=(0,-71,-2.13e-14) rot=(1,0,0;0.785398rad)
  Support = -> [DatumPlane007]
  expr: Constraints[0] = <<sp>>.insertFavDistAuZeroDuPLan
  expr: Constraints[19] = <<sp>>.epaisseurParois
  expr: Constraints[20] = <<sp>>.favEpBordure
  expr: Constraints[21] = <<sp>>.favDistBordPlan
  expr: Constraints[22] = <<sp>>.largeurModuleBase - 2 * <<sp>>.epaisseurParois
  expr: Constraints[23] = <<sp>>.favEpBordure
  expr: Constraints[24] = <<sp>>.Face - <<sp>>.epaisseurParois
  expr: Constraints[25] = <<sp>>.favEpBordure
  sketch-geometry (9):
    g0: GeomPoint X=0 Y=4.24264 Z=0
    g1: LineSegment StartX=-112.5 StartY=20.9853 StartZ=0 EndX=-112.5 EndY=81.7426 EndZ=0
    g2: LineSegment StartX=-112.5 StartY=81.7426 StartZ=0 EndX=-2.5 EndY=81.7426 EndZ=0
    g3: LineSegment StartX=-2.5 StartY=81.7426 StartZ=0 EndX=-2.5 EndY=20.9853 EndZ=0
    g4: LineSegment StartX=-2.5 StartY=20.9853 StartZ=0 EndX=-4 EndY=20.9853 EndZ=0
    g5: LineSegment StartX=-4 StartY=20.9853 StartZ=0 EndX=-4 EndY=80.2426 EndZ=0
    g6: LineSegment StartX=-4 StartY=80.2426 StartZ=0 EndX=-111 EndY=80.2426 EndZ=0
    g7: LineSegment StartX=-111 StartY=80.2426 StartZ=0 EndX=-111 EndY=20.9853 EndZ=0
    g8: LineSegment StartX=-111 StartY=20.9853 StartZ=0 EndX=-112.5 EndY=20.9853 EndZ=0
  constraints (26):
    c: DistanceY(g-1,g0) = 4.24264
    c: Vertical(g0,g-1)
    c: Vertical(g1)
    c: Coincident(g1,g2)
    c: Horizontal(g2)
    c: Coincident(g2,g3)
    c: Vertical(g3)
    c: Coincident(g3,g4)
    c: Horizontal(g4)
    c: Coincident(g4,g5)
    c: Vertical(g5)
    c: Coincident(g5,g6)
    c: Horizontal(g6)
    c: Coincident(g6,g7)
    c: Vertical(g7)
    c: Coincident(g7,g8)
    c: Coincident(g8,g1)
    c: Horizontal(g8)
    c: Horizontal(g7,g4)
    c: DistanceX(g3,g0) = 2.5
    c: DistanceX(g4,g4) = 1.5
    c: DistanceY(g0,g3) = 16.7426
    c: DistanceX(g1,g3) = 110
    c: DistanceY(g5,g2) = 1.5
    c: DistanceY(g0,g2) = 77.5
    c: DistanceX(g1,g7) = 1.5
FEATURE [PartDesign::Pad] Pad014  label="favRebordSupport"
  AllowMultiFace = false
  BaseFeature = -> Pocket010
  Direction = (1,1,1)
  Length = 10
  Length2 = 100
  Profile = -> Sketch030
  Type = 3
  UpToFace = -> Pocket010 [Face13]
FEATURE [PartDesign::Pad] Pad015  label="favRebord"
  AllowMultiFace = false
  BaseFeature = -> Pad014
  Direction = (1,1,1)
  Length = 4.15
  Length2 = 100
  Profile = -> Sketch030
  Reversed = true
  Type = 0
  expr: Length = <<sp>>.favBordureProf
FEATURE [Sketcher::SketchObject] Sketch031  label="sk_bourlet"
  ExternalGeometry = -> [Pad015]
  FullyConstrained = true
  MapMode = 5
  Placement = pos=(-2.5,0,0) rot=(0.57735,0.57735,0.57735;2.0944rad)
  Support = -> [Pad015]
  expr: Constraints[3] = <<sp>>.bourletMaintientRayon - <<sp>>.bourletRayonJeu
  sketch-geometry (2):
    g0: ArcOfCircle CenterX=-11.184 CenterY=55.7855 CenterZ=0 NormalX=0 NormalY=0 NormalZ=1 AngleXU=0 Radius=1.3 StartAngle=5.49779 EndAngle=8.63938
    g1: LineSegment StartX=-12.1032 StartY=56.7048 StartZ=0 EndX=-10.2647 EndY=54.8663 EndZ=0
  constraints (6):
    c: Coincident(g0,g-3)
    c: PointOnObject(g0,g-3)
    c: PointOnObject(g0,g-3)
    c: Radius(g0) = 1.3
    c: Coincident(g1,g0)
    c: Coincident(g1,g0)
FEATURE [PartDesign::Pad] Pad016  label="bourlet"
  AllowMultiFace = false
  BaseFeature = -> Pad015
  Direction = (1,1,1)
  Length = 10
  Length2 = 100
  Profile = -> Sketch031
  Reversed = true
  Type = 3
  UpToFace = -> Pad015 [Face11]
FEATURE [Sketcher::SketchObject] Sketch040  label="sk_trouFav"
  FullyConstrained = true
  MapMode = 5
  Placement = pos=(0,-93.2843,-2.84e-14) rot=(1,0,0;0.785398rad)
  Support = -> [DatumPlane011]
  expr: Constraints[16] = <<sp>>.distZeroPlanFAV
  expr: Constraints[18] = <<SW_C1500AT>>.trouLargeur
  expr: Constraints[19] = <<SW_C1500AT>>.trouLongeur
  expr: Constraints[20] = <<favPos>>.SwitchPosX
  expr: Constraints[21] = <<favPos>>.switchPosY
  expr: Constraints[22] = <<KTD132>>.trouLongeur + <<KTD132>>.trouJeuLong
  expr: Constraints[23] = <<KTD132>>.trouLargeur + <<KTD132>>.trouJeuLarg
  expr: Constraints[24] = <<favPos>>.ecranPosX
  expr: Constraints[25] = <<favPos>>.ecranPosY
  expr: Constraints[26] = <<favPos>>.FusePosX
  expr: Constraints[27] = <<favPos>>.FusePosY
  expr: Constraints[28] = <<fuse>>.corpsPercageDiam + <<fuse>>.corpsPercageJeu
  expr: Constraints[40] = <<fuse>>.corpsLargeurMeplat + <<fuse>>.corpsPercageJeu
  sketch-geometry (14):
    g0: LineSegment StartX=-92.1 StartY=95.4 StartZ=0 EndX=-5 EndY=95.4 EndZ=0
    g1: LineSegment StartX=-5 StartY=95.4 StartZ=0 EndX=-5 EndY=50 EndZ=0
    g2: LineSegment StartX=-5 StartY=50 StartZ=0 EndX=-92.1 EndY=50 EndZ=0
    g3: LineSegment StartX=-92.1 StartY=50 StartZ=0 EndX=-92.1 EndY=95.4 EndZ=0
    g4: LineSegment StartX=-108.55 StartY=83.25 StartZ=0 EndX=-97 EndY=83.25 EndZ=0
    g5: LineSegment StartX=-97 StartY=83.25 StartZ=0 EndX=-97 EndY=55 EndZ=0
    g6: LineSegment StartX=-97 StartY=55 StartZ=0 EndX=-108.55 EndY=55 EndZ=0
    g7: LineSegment StartX=-108.55 StartY=55 StartZ=0 EndX=-108.55 EndY=83.25 EndZ=0
    g8: ArcOfCircle CenterX=-85 CenterY=35 CenterZ=0 NormalX=0 NormalY=0 NormalZ=1 AngleXU=0 Radius=6.85 StartAngle=3.65999 EndAngle=5.76479
    g9: GeomPoint X=0 Y=20 Z=0
    g10: LineSegment StartX=-90.95 StartY=38.3941 StartZ=0 EndX=-90.95 EndY=31.6059 EndZ=0
    g11: LineSegment StartX=-79.05 StartY=31.6059 StartZ=0 EndX=-79.05 EndY=38.3941 EndZ=0
    g12: LineSegment StartX=-90.95 StartY=38.3941 StartZ=0 EndX=-79.05 EndY=38.3941 EndZ=0
    g13: ArcOfCircle CenterX=-85 CenterY=35 CenterZ=0 NormalX=0 NormalY=0 NormalZ=1 AngleXU=0 Radius=6.85 StartAngle=0.5184 EndAngle=2.62319
  constraints (41):
    c: Coincident(g0,g1)
    c: Coincident(g1,g2)
    c: Coincident(g2,g3)
    c: Coincident(g3,g0)
    c: Horizontal(g0)
    c: Horizontal(g2)
    c: Vertical(g1)
    c: Vertical(g3)
    c: Coincident(g4,g5)
    c: Coincident(g5,g6)
    c: Coincident(g6,g7)
    c: Coincident(g7,g4)
    c: Horizontal(g4)
    c: Horizontal(g6)
    c: Vertical(g5)
    c: Vertical(g7)
    c: DistanceY(g-1,g9) = 20
    c: Vertical(g-1,g9)
    c: DistanceX(g4,g4) = 11.55
    c: DistanceY(g7,g7) = 28.25
    c: DistanceX(g5,g9) = 97
    c: DistanceY(g9,g5) = 35
    c: DistanceX(g0,g0) = 87.1
    c: DistanceY(g1,g1) = 45.4
    c: DistanceX(g1,g9) = 5
    c: DistanceY(g9,g1) = 30
    c: DistanceX(g8,g9) = 85
    c: DistanceY(g9,g8) = 15
    c: Diameter(g8) = 13.7
    c: Vertical(g10)
    c: Vertical(g11)
    c: Coincident(g12,g10)
    c: Coincident(g12,g11)
    c: Horizontal(g12)
    c: Coincident(g8,g10)
    c: Coincident(g13,g10)
    c: Equal(g8,g13)
    c: Coincident(g8,g11)
    c: Coincident(g13,g11)
    c: Coincident(g8,g13)
    c: DistanceX(g12,g12) = 11.9
FEATURE [PartDesign::Pocket] Pocket022  label="favPercee"
  BaseFeature = -> Pad016
  Direction = (1,1,1)
  Length = 5
  Length2 = 100
  Profile = -> Sketch040
  Type = 1
FEATURE [PartDesign::Body] Body002  label="faceAvant"
  BaseFeature = -> Slice_child1
  Group = -> [Clone001,Thickness001,DatumPlane007,Sketch016,Pad005,Sketch017,Pad006,Sketch018,Pocket010,DatumPlane011,Sketch030,Pad014,Pad015,Sketch031,Pad016,Sketch040,Pocket022]
  Origin = -> Origin003
  Tip = -> Pocket022
COMPONENT P2 — recipe-attached ("visTHCM3x10_001", modeled in this document).
Construction recipe (the document's own serialized feature program — sketch geometry with constraints, then the solid features built on it; lengths are millimeters unless a unit is written):

FEATURE [Sketcher::SketchObject] Sketch020
  FullyConstrained = false
  MapMode = 5
  Support = -> [XY_Plane006]
  sketch-geometry (1):
    g0: Circle CenterX=0 CenterY=0 CenterZ=0 NormalX=0 NormalY=0 NormalZ=1 AngleXU=0 Radius=2.75
  constraints (2):
    c: Coincident(g0,g-1)
    c: Diameter(g0) = 5.5
FEATURE [PartDesign::Pad] Pad008  label="tete"
  AllowMultiFace = false
  Direction = (1,1,1)
  Length = 3
  Length2 = 100
  Profile = -> Sketch020
  Type = 0
FEATURE [Sketcher::SketchObject] Sketch001
  FullyConstrained = false
  MapMode = 5
  Placement = pos=(0,0,0) rot=(1,0,0;3.14159rad)
  Support = -> [Pad008]
  sketch-geometry (1):
    g0: Circle CenterX=0 CenterY=0 CenterZ=0 NormalX=0 NormalY=0 NormalZ=1 AngleXU=0 Radius=1.5
  constraints (2):
    c: Coincident(g0,g-1)
    c: Diameter(g0) = 3
FEATURE [PartDesign::Pad] Pad009  label="corps"
  AllowMultiFace = false
  BaseFeature = -> Pad008
  Direction = (1,1,1)
  Length = 10
  Length2 = 100
  Profile = -> Sketch001
  Type = 0
FEATURE [PartDesign::Plane] DatumPlane008
  AttachmentOffset = pos=(0,0,3) rot=(0,0,1;0rad)
  Length = 60
  MapMode = 5
  Placement = pos=(0,0,3) rot=(0,0,1;0rad)
  ResizeMode = 0
  Support = -> [XY_Plane006]
  Width = 60
FEATURE [Sketcher::SketchObject] Sketch021
  FullyConstrained = false
  MapMode = 5
  Placement = pos=(0,0,3) rot=(0,0,1;0rad)
  Support = -> [DatumPlane008]
  sketch-geometry (7):
    g0: LineSegment StartX=0.721688 StartY=-1.25 StartZ=0 EndX=1.44338 EndY=1.0119e-12 EndZ=0
    g1: LineSegment StartX=1.44338 StartY=1.0119e-12 StartZ=0 EndX=0.721688 EndY=1.25 EndZ=0
    g2: LineSegment StartX=0.721688 StartY=1.25 StartZ=0 EndX=-0.721688 EndY=1.25 EndZ=0
    g3: LineSegment StartX=-0.721688 StartY=1.25 StartZ=0 EndX=-1.44338 EndY=8.689e-13 EndZ=0
    g4: LineSegment StartX=-1.44338 StartY=8.689e-13 StartZ=0 EndX=-0.721688 EndY=-1.25 EndZ=0
    g5: LineSegment StartX=-0.721688 StartY=-1.25 StartZ=0 EndX=0.721688 EndY=-1.25 EndZ=0
    g6: Circle CenterX=0 CenterY=0 CenterZ=0 NormalX=0 NormalY=0 NormalZ=1 AngleXU=0 Radius=1.44338
  constraints (16):
    c: Coincident(g0,g1)
    c: Coincident(g1,g2)
    c: Coincident(g2,g3)
    c: Coincident(g3,g4)
    c: Coincident(g4,g5)
    c: Coincident(g5,g0)
    c: Equal(g0, g1-g5) x5
    c: PointOnObject(g0,g6)
    c: PointOnObject(g1,g6)
    c: PointOnObject(g2,g6)
    c: PointOnObject(g3,g6)
    c: PointOnObject(g4,g6)
    c: PointOnObject(g5,g6)
    c: Coincident(g6,g-1)
    c: Horizontal(g2)
    c: DistanceY(g0,g1) = 2.5
FEATURE [PartDesign::Pocket] Pocket011  label="emprunte"
  AllowMultiFace = false
  BaseFeature = -> Pad009
  Direction = (1,1,1)
  Length = 4
  Length2 = 100
  Profile = -> Sketch021
  Type = 0
FEATURE [PartDesign::Body] Body003  label="visTHCM3x10_001"
  Group = -> [Sketch020,Pad008,Sketch001,Pad009,DatumPlane008,Sketch021,Pocket011]
  Origin = -> Origin010
  Placement = pos=(-6.5,-61.582,5.72756) rot=(1,0,0;3.92699rad)
  Tip = -> Pocket011
COMPONENT P3 — recipe-attached ("visTHCM3x10_002", modeled in this document).
Construction recipe (the document's own serialized feature program — sketch geometry with constraints, then the solid features built on it; lengths are millimeters unless a unit is written):

FEATURE [PartDesign::Plane] DatumPlane009
  AttachmentOffset = pos=(0,0,3) rot=(0,0,1;0rad)
  Length = 60
  MapMode = 5
  Placement = pos=(0,0,3) rot=(0,0,1;0rad)
  ResizeMode = 0
  Support = -> [XY_Plane007]
  Width = 60
FEATURE [Sketcher::SketchObject] Sketch022
  FullyConstrained = false
  MapMode = 5
  Support = -> [XY_Plane007]
  sketch-geometry (1):
    g0: Circle CenterX=0 CenterY=0 CenterZ=0 NormalX=0 NormalY=0 NormalZ=1 AngleXU=0 Radius=2.75
  constraints (2):
    c: Coincident(g0,g-1)
    c: Diameter(g0) = 5.5
FEATURE [PartDesign::Pad] Pad011  label="tete001"
  AllowMultiFace = false
  Direction = (1,1,1)
  Length = 3
  Length2 = 100
  Profile = -> Sketch022
  Type = 0
FEATURE [Sketcher::SketchObject] Sketch023
  FullyConstrained = false
  MapMode = 5
  Placement = pos=(0,0,0) rot=(1,0,0;3.14159rad)
  Support = -> [Pad011]
  sketch-geometry (1):
    g0: Circle CenterX=0 CenterY=0 CenterZ=0 NormalX=0 NormalY=0 NormalZ=1 AngleXU=0 Radius=1.5
  constraints (2):
    c: Coincident(g0,g-1)
    c: Diameter(g0) = 3
FEATURE [PartDesign::Pad] Pad010  label="corps001"
  AllowMultiFace = false
  BaseFeature = -> Pad011
  Direction = (1,1,1)
  Length = 10
  Length2 = 100
  Profile = -> Sketch023
  Type = 0
FEATURE [Sketcher::SketchObject] Sketch024
  FullyConstrained = false
  MapMode = 5
  Placement = pos=(0,0,3) rot=(0,0,1;0rad)
  Support = -> [DatumPlane009]
  sketch-geometry (7):
    g0: LineSegment StartX=0.721688 StartY=-1.25 StartZ=0 EndX=1.44338 EndY=1.0119e-12 EndZ=0
    g1: LineSegment StartX=1.44338 StartY=1.0119e-12 StartZ=0 EndX=0.721688 EndY=1.25 EndZ=0
    g2: LineSegment StartX=0.721688 StartY=1.25 StartZ=0 EndX=-0.721688 EndY=1.25 EndZ=0
    g3: LineSegment StartX=-0.721688 StartY=1.25 StartZ=0 EndX=-1.44338 EndY=8.689e-13 EndZ=0
    g4: LineSegment StartX=-1.44338 StartY=8.689e-13 StartZ=0 EndX=-0.721688 EndY=-1.25 EndZ=0
    g5: LineSegment StartX=-0.721688 StartY=-1.25 StartZ=0 EndX=0.721688 EndY=-1.25 EndZ=0
    g6: Circle CenterX=0 CenterY=0 CenterZ=0 NormalX=0 NormalY=0 NormalZ=1 AngleXU=0 Radius=1.44338
  constraints (16):
    c: Coincident(g0,g1)
    c: Coincident(g1,g2)
    c: Coincident(g2,g3)
    c: Coincident(g3,g4)
    c: Coincident(g4,g5)
    c: Coincident(g5,g0)
    c: Equal(g0, g1-g5) x5
    c: PointOnObject(g0,g6)
    c: PointOnObject(g1,g6)
    c: PointOnObject(g2,g6)
    c: PointOnObject(g3,g6)
    c: PointOnObject(g4,g6)
    c: PointOnObject(g5,g6)
    c: Coincident(g6,g-1)
    c: Horizontal(g2)
    c: DistanceY(g0,g1) = 2.5
FEATURE [PartDesign::Pocket] Pocket012  label="emprunte001"
  AllowMultiFace = false
  BaseFeature = -> Pad010
  Direction = (1,1,1)
  Length = 4
  Length2 = 100
  Profile = -> Sketch024
  Type = 0
FEATURE [PartDesign::Body] Body004  label="visTHCM3x10_002"
  Group = -> [Sketch022,Pad011,Sketch023,Pad010,DatumPlane009,Sketch024,Pocket012]
  Origin = -> Origin011
  Placement = pos=(-108.5,-61.582,5.72756) rot=(1,0,0;3.92699rad)
  Tip = -> Pocket012
COMPONENT P4 — recipe-attached ("DC5525", modeled in this document).
Construction recipe (the document's own serialized feature program — sketch geometry with constraints, then the solid features built on it; lengths are millimeters unless a unit is written):

FEATURE [Sketcher::SketchObject] Sketch  label="profileDeBase"
  FullyConstrained = true
  MapMode = 5
  Placement = pos=(0,0,0) rot=(0.57735,0.57735,0.57735;2.0944rad)
  Support = -> [YZ_Plane001]
  expr: Constraints[10] = <<sp>>.petitRetour
  expr: Constraints[11] = <<sp>>.angleFacePetitRetour
  expr: Constraints[12] = <<sp>>.Face
  expr: Constraints[13] = <<sp>>.angleFaceRetourHaut
  expr: Constraints[8] = <<sp>>.Base
  expr: Constraints[9] = <<sp>>.anglePetitRetourBase
  sketch-geometry (5):
    g0: LineSegment StartX=0 StartY=0 StartZ=0 EndX=-65 EndY=0 EndZ=0
    g1: LineSegment StartX=-65 StartY=0 StartZ=0 EndX=-79.1421 EndY=14.1421 EndZ=0
    g2: LineSegment StartX=-79.1421 StartY=14.1421 StartZ=0 EndX=-22.5736 EndY=70.7107 EndZ=0
    g3: LineSegment StartX=-22.5736 StartY=70.7107 StartZ=0 EndX=0 EndY=48.1371 EndZ=0
    g4: LineSegment StartX=0 StartY=48.1371 StartZ=0 EndX=0 EndY=0 EndZ=0
  constraints (14):
    c: Coincident(g-1,g0)
    c: Horizontal(g0)
    c: Coincident(g0,g1)
    c: Coincident(g1,g2)
    c: Coincident(g2,g3)
    c: PointOnObject(g3,g-2)
    c: Coincident(g3,g4)
    c: Coincident(g4,g0)
    c: DistanceX(g0,g0) = 65
    c: Angle(g0,g1) = 2.35619
    c: Distance(g1) = 20
    c: Angle(g1,g2) = 1.5708
    c: Distance(g2) = 80
    c: Angle(g2,g3) = 1.5708
FEATURE [PartDesign::Pad] Pad
  AllowMultiFace = false
  Direction = (1,1,1)
  Length = 115
  Length2 = 100
  Placement = pos=(0,0,0) rot=(0.57735,0.57735,0.57735;2.0944rad)
  Profile = -> Sketch
  Reversed = true
  Type = 0
  expr: Length = <<sp>>.largeurModuleBase
FEATURE [PartDesign::Plane] DatumPlane
  AttachmentOffset = pos=(71,0,0) rot=(0,-1,0;0.785398rad)
  Length = 98.6412
  MapMode = 5
  Placement = pos=(-7.9e-15,8e-15,71) rot=(0.678598,0.678598,0.281085;3.68962rad)
  ResizeMode = 0
  Support = -> [Pad]
  Width = 63.0813
FEATURE [PartDesign::Body] Body  label="Base"
  Group = -> [Sketch,Pad,DatumPlane]
  Origin = -> Origin001
  Tip = -> Pad
COMPONENT P5 — same part as P4; its construction recipe is shown at P4.
COMPONENT P6 — geometry summary ("xt60fem"; no construction recipe available for this part):
  bounding box: 20.5 x 16.5 x 7.5 mm
  tessellated surface: 23,736 triangles
  volume: 955 mm^3 (38% of its bounding box)
COMPONENT P7 — geometry summary ("xt60Male"; no construction recipe available for this part):
  bounding box: 20.2 x 16.6 x 7.5 mm
  tessellated surface: 14,992 triangles
  volume: 1201 mm^3 (48% of its bounding box)
COMPONENT P8 — geometry summary ("ZSB_RUTHEX_M3_5.7_001"; no construction recipe available for this part):
  bounding box: 5.7 x 4.6 x 4.6 mm
  tessellated surface: 4,640 triangles
  volume: 44 mm^3 (36% of its bounding box)
  symmetry: 4-fold rotationally symmetric about the y axis; mirror-symmetric across its x mid-plane, z mid-plane
COMPONENT P9 — geometry summary ("ZSB_RUTHEX_M3_5.7_002"; no construction recipe available for this part):
  bounding box: 5.7 x 4.6 x 4.6 mm
  tessellated surface: 4,640 triangles
  volume: 44 mm^3 (36% of its bounding box)
  symmetry: 4-fold rotationally symmetric about the y axis; mirror-symmetric across its x mid-plane, z mid-plane
COMPONENT P10 — geometry summary ("ZSB_RUTHEX_M3_5.7_003"; no construction recipe available for this part):
  bounding box: 6.9 x 6.9 x 4.6 mm
  tessellated surface: 4,640 triangles
  volume: 44 mm^3 (20% of its bounding box)
  symmetry: mirror-symmetric across its x mid-plane
COMPONENT P11 — geometry summary ("ZSB_RUTHEX_M3_5.7_004"; no construction recipe available for this part):
  bounding box: 6.9 x 6.9 x 4.6 mm
  tessellated surface: 4,640 triangles
  volume: 44 mm^3 (20% of its bounding box)
  symmetry: mirror-symmetric across its x mid-plane
COMPONENT P12 — recipe-attached ("partVisPointeauM3x10_001", modeled in this document).
Construction recipe (the document's own serialized feature program — sketch geometry with constraints, then the solid features built on it; lengths are millimeters unless a unit is written):

FEATURE [Sketcher::SketchObject] Sketch025
  FullyConstrained = false
  MapMode = 5
  Support = -> [XY_Plane008]
  sketch-geometry (1):
    g0: Circle CenterX=0 CenterY=0 CenterZ=0 NormalX=0 NormalY=0 NormalZ=1 AngleXU=0 Radius=1.5
  constraints (2):
    c: Coincident(g0,g-1)
    c: Diameter(g0) = 3
FEATURE [Sketcher::SketchObject] Sketch026
  FullyConstrained = false
  MapMode = 5
  Support = -> [XY_Plane008]
  sketch-geometry (7):
    g0: LineSegment StartX=0.433013 StartY=-0.75 StartZ=0 EndX=0.866025 EndY=1.25568e-11 EndZ=0
    g1: LineSegment StartX=0.866025 StartY=1.25568e-11 StartZ=0 EndX=0.433013 EndY=0.75 EndZ=0
    g2: LineSegment StartX=0.433013 StartY=0.75 StartZ=0 EndX=-0.433013 EndY=0.75 EndZ=0
    g3: LineSegment StartX=-0.433013 StartY=0.75 StartZ=0 EndX=-0.866025 EndY=2.91366e-11 EndZ=0
    g4: LineSegment StartX=-0.866025 StartY=2.91366e-11 StartZ=0 EndX=-0.433013 EndY=-0.75 EndZ=0
    g5: LineSegment StartX=-0.433013 StartY=-0.75 StartZ=0 EndX=0.433013 EndY=-0.75 EndZ=0
    g6: Circle CenterX=0 CenterY=0 CenterZ=0 NormalX=0 NormalY=0 NormalZ=1 AngleXU=0 Radius=0.866025
  constraints (16):
    c: Coincident(g0,g1)
    c: Coincident(g1,g2)
    c: Coincident(g2,g3)
    c: Coincident(g3,g4)
    c: Coincident(g4,g5)
    c: Coincident(g5,g0)
    c: Equal(g0, g1-g5) x5
    c: PointOnObject(g0,g6)
    c: PointOnObject(g1,g6)
    c: PointOnObject(g2,g6)
    c: PointOnObject(g3,g6)
    c: PointOnObject(g4,g6)
    c: PointOnObject(g5,g6)
    c: Coincident(g6,g-1)
    c: Horizontal(g2)
    c: DistanceY(g0,g1) = 1.5
FEATURE [PartDesign::Pad] Pad012
  AllowMultiFace = false
  Direction = (1,1,1)
  Length = 10
  Length2 = 100
  Profile = -> Sketch025
  Type = 0
FEATURE [PartDesign::Chamfer] Chamfer
  Angle = 45
  Base = -> Pad012 [Edge3]
  BaseFeature = -> Pad012
  ChamferType = 0
  FlipDirection = false
  Size = 1.4
  Size2 = 1
  SupportTransform = false
  UseAllEdges = false
FEATURE [PartDesign::Pocket] Pocket013
  AllowMultiFace = false
  BaseFeature = -> Chamfer
  Direction = (1,1,1)
  Length = 1.5
  Length2 = 100
  Profile = -> Sketch026
  Reversed = true
  Type = 0
FEATURE [PartDesign::Chamfer] Chamfer001
  Angle = 45
  Base = -> Pocket013 [Edge3]
  BaseFeature = -> Pocket013
  ChamferType = 0
  FlipDirection = false
  Size = 0.1
  Size2 = 1
  SupportTransform = false
  UseAllEdges = false
FEATURE [PartDesign::Body] Body005  label="bodyVisPointeauM3x10_001"
  Group = -> [Sketch025,Pad012,Chamfer,Sketch026,Pocket013,Chamfer001]
  Origin = -> Origin013
  Tip = -> Chamfer001
COMPONENT P13 — recipe-attached ("partVisPointeauM3x10_002", modeled in this document).
Construction recipe (the document's own serialized feature program — sketch geometry with constraints, then the solid features built on it; lengths are millimeters unless a unit is written):

FEATURE [Sketcher::SketchObject] Sketch027
  FullyConstrained = false
  MapMode = 5
  Support = -> [XY_Plane010]
  sketch-geometry (7):
    g0: LineSegment StartX=0.433013 StartY=-0.75 StartZ=0 EndX=0.866025 EndY=1.25568e-11 EndZ=0
    g1: LineSegment StartX=0.866025 StartY=1.25568e-11 StartZ=0 EndX=0.433013 EndY=0.75 EndZ=0
    g2: LineSegment StartX=0.433013 StartY=0.75 StartZ=0 EndX=-0.433013 EndY=0.75 EndZ=0
    g3: LineSegment StartX=-0.433013 StartY=0.75 StartZ=0 EndX=-0.866025 EndY=2.91366e-11 EndZ=0
    g4: LineSegment StartX=-0.866025 StartY=2.91366e-11 StartZ=0 EndX=-0.433013 EndY=-0.75 EndZ=0
    g5: LineSegment StartX=-0.433013 StartY=-0.75 StartZ=0 EndX=0.433013 EndY=-0.75 EndZ=0
    g6: Circle CenterX=0 CenterY=0 CenterZ=0 NormalX=0 NormalY=0 NormalZ=1 AngleXU=0 Radius=0.866025
  constraints (16):
    c: Coincident(g0,g1)
    c: Coincident(g1,g2)
    c: Coincident(g2,g3)
    c: Coincident(g3,g4)
    c: Coincident(g4,g5)
    c: Coincident(g5,g0)
    c: Equal(g0, g1-g5) x5
    c: PointOnObject(g0,g6)
    c: PointOnObject(g1,g6)
    c: PointOnObject(g2,g6)
    c: PointOnObject(g3,g6)
    c: PointOnObject(g4,g6)
    c: PointOnObject(g5,g6)
    c: Coincident(g6,g-1)
    c: Horizontal(g2)
    c: DistanceY(g0,g1) = 1.5
FEATURE [Sketcher::SketchObject] Sketch028
  FullyConstrained = false
  MapMode = 5
  Support = -> [XY_Plane010]
  sketch-geometry (1):
    g0: Circle CenterX=0 CenterY=0 CenterZ=0 NormalX=0 NormalY=0 NormalZ=1 AngleXU=0 Radius=1.5
  constraints (2):
    c: Coincident(g0,g-1)
    c: Diameter(g0) = 3
FEATURE [PartDesign::Pad] Pad013
  AllowMultiFace = false
  Direction = (1,1,1)
  Length = 10
  Length2 = 100
  Profile = -> Sketch028
  Type = 0
FEATURE [PartDesign::Chamfer] Chamfer003
  Angle = 45
  Base = -> Pad013 [Edge3]
  BaseFeature = -> Pad013
  ChamferType = 0
  FlipDirection = false
  Size = 1.4
  Size2 = 1
  SupportTransform = false
  UseAllEdges = false
FEATURE [PartDesign::Pocket] Pocket014
  AllowMultiFace = false
  BaseFeature = -> Chamfer003
  Direction = (1,1,1)
  Length = 1.5
  Length2 = 100
  Profile = -> Sketch027
  Reversed = true
  Type = 0
FEATURE [PartDesign::Chamfer] Chamfer002
  Angle = 45
  Base = -> Pocket014 [Edge3]
  BaseFeature = -> Pocket014
  ChamferType = 0
  FlipDirection = false
  Size = 0.1
  Size2 = 1
  SupportTransform = false
  UseAllEdges = false
FEATURE [PartDesign::Body] Body006  label="bodyVisPointeauM3x10_002"
  Group = -> [Sketch028,Pad013,Chamfer003,Sketch027,Pocket014,Chamfer002]
  Origin = -> Origin015
  Tip = -> Chamfer002
COMPONENT P14 — recipe-attached ("tigeLaiton001", modeled in this document).
Construction recipe (the document's own serialized feature program — sketch geometry with constraints, then the solid features built on it; lengths are millimeters unless a unit is written):

FEATURE [PartDesign::Plane] DatumPlane012  label="planBaseTige"
  AttachmentOffset = pos=(0,0,-5.18) rot=(0,0,1;0rad)
  Length = 60
  MapMode = 5
  Placement = pos=(-5.18,1.2e-15,-1.2e-15) rot=(0.57735,0.57735,0.57735;2.0944rad)
  ResizeMode = 0
  Support = -> [YZ_Plane012]
  Width = 60
  expr: .AttachmentOffset.Base.z = -<<tige>>.planBaseTigeposX
FEATURE [Sketcher::SketchObject] Sketch032  label="sk_tiges"
  FullyConstrained = true
  MapMode = 5
  Placement = pos=(-5.18,1.2e-15,-1.2e-15) rot=(0.57735,0.57735,0.57735;2.0944rad)
  Support = -> [DatumPlane012]
  expr: Constraints[0] = <<tige>>.tigeDiam
  expr: Constraints[1] = <<tige>>.tigePosY
  expr: Constraints[2] = <<tige>>.tigePosX
  sketch-geometry (1):
    g0: Circle CenterX=-14 CenterY=14.3 CenterZ=0 NormalX=0 NormalY=0 NormalZ=1 AngleXU=0 Radius=1.25
  constraints (3):
    c: Diameter(g0) = 2.5
    c: DistanceY(g-1,g0) = 14.3
    c: DistanceX(g0,g-1) = 14
FEATURE [PartDesign::Pad] Pad017  label="tigeBasse"
  AllowMultiFace = false
  Direction = (1,1,1)
  Length = 98.62
  Length2 = 100
  Placement = pos=(-5.18,1e-15,-1e-15) rot=(0.57735,0.57735,0.57735;2.0944rad)
  Profile = -> Sketch032
  Reversed = true
  Type = 0
  expr: Length = <<tige>>.tigeLong
FEATURE [PartDesign::Body] Body007  label="tigeLaiton"
  Group = -> [DatumPlane012,Sketch032,Pad017]
  Origin = -> Origin016
  Tip = -> Pad017
FEATURE [PartDesign::Plane] DatumPlane013  label="planTige2"
  AttachmentOffset = pos=(0,0,-5.18) rot=(0,0,1;0rad)
  Length = 60
  MapMode = 5
  Placement = pos=(-5.18,1.2e-15,-1.2e-15) rot=(0.57735,0.57735,0.57735;2.0944rad)
  ResizeMode = 0
  Support = -> [YZ_Plane014]
  Width = 60
  expr: .AttachmentOffset.Base.z = -<<tige>>.planBaseTigeposX
FEATURE [Sketcher::SketchObject] Sketch033  label="sk_tige2"
  FullyConstrained = true
  MapMode = 5
  Placement = pos=(-5.18,1.2e-15,-1.2e-15) rot=(0.57735,0.57735,0.57735;2.0944rad)
  Support = -> [DatumPlane013]
  expr: Constraints[0] = <<tige>>.tigeDiam
  expr: Constraints[1] = <<tige>>.tigePosX
  expr: Constraints[2] = <<tige>>.tigePosY + <<tige>>.xtEcartBroches
  sketch-geometry (1):
    g0: Circle CenterX=-14 CenterY=21.86 CenterZ=0 NormalX=0 NormalY=0 NormalZ=1 AngleXU=0 Radius=1.25
  constraints (3):
    c: Diameter(g0) = 2.5
    c: DistanceX(g0,g-1) = 14
    c: DistanceY(g-1,g0) = 21.86
FEATURE [PartDesign::Pad] Pad018
  AllowMultiFace = false
  Direction = (1,1,1)
  Length = 98.62
  Length2 = 100
  Placement = pos=(-5.18,1e-15,-1e-15) rot=(0.57735,0.57735,0.57735;2.0944rad)
  Profile = -> Sketch033
  Reversed = true
  Type = 0
  expr: Length = <<tige>>.tigeLong
FEATURE [PartDesign::Body] Body008  label="tige2"
  Group = -> [DatumPlane013,Sketch033,Pad018]
  Origin = -> Origin018
  Tip = -> Pad018
COMPONENT P15 — recipe-attached ("porteFuse", modeled in this document).
Construction recipe (the document's own serialized feature program — sketch geometry with constraints, then the solid features built on it; lengths are millimeters unless a unit is written):

FEATURE [Sketcher::SketchObject] Sketch041
  FullyConstrained = false
  MapMode = 5
  Placement = pos=(0,0,0) rot=(1,0,0;1.5708rad)
  Support = -> [XZ_Plane042]
  expr: Constraints[20] = <<fuse>>.corpsDiamExt / 2
  expr: Constraints[22] = <<fuse>>.corpsHautTot
  expr: Constraints[23] = <<fuse>>.CorpsLongFutInferier
  expr: Constraints[24] = <<fuse>>.corpsDiamFutInferieur / 2
  expr: Constraints[26] = <<fuse>>.corpsDiamFilletage / 2
  expr: Constraints[27] = <<fuse>>.corpsLevreHauteur
  expr: Constraints[28] = <<fuse>>.corpsHauteurFilletage
  sketch-geometry (11):
    g0: LineSegment StartX=3.565 StartY=-12 StartZ=0 EndX=3.565 EndY=0 EndZ=0
    g1: LineSegment StartX=3.565 StartY=0 StartZ=0 EndX=7.5 EndY=0 EndZ=0
    g2: LineSegment StartX=7.5 StartY=0 StartZ=0 EndX=7.5 EndY=-3 EndZ=0
    g3: LineSegment StartX=7.5 StartY=-3 StartZ=0 EndX=5.85 EndY=-3 EndZ=0
    g4: LineSegment StartX=5.85 StartY=-3 StartZ=0 EndX=5.85 EndY=-11 EndZ=0
    g5: LineSegment StartX=5.85 StartY=-11 StartZ=0 EndX=5.5925 EndY=-12.7105 EndZ=0
    g6: LineSegment StartX=5.5925 StartY=-12.7105 StartZ=0 EndX=4.335 EndY=-14.2 EndZ=0
    g7: LineSegment StartX=4.335 StartY=-14.2 StartZ=0 EndX=4.335 EndY=-24 EndZ=0
    g8: LineSegment StartX=4.335 StartY=-24 StartZ=0 EndX=0 EndY=-24 EndZ=0
    g9: LineSegment StartX=3.565 StartY=-12 StartZ=0 EndX=0 EndY=-12 EndZ=0
    g10: LineSegment StartX=0 StartY=-12 StartZ=0 EndX=0 EndY=-24 EndZ=0
  constraints (33):
    c: PointOnObject(g0,g-1)
    c: Vertical(g0)
    c: Coincident(g0,g1)
    c: PointOnObject(g1,g-1)
    c: Coincident(g1,g2)
    c: Coincident(g2,g3)
    c: Coincident(g3,g4)
    c: Vertical(g4)
    c: Coincident(g4,g5)
    c: Coincident(g5,g6)
    c: Coincident(g6,g7)
    c: Vertical(g7)
    c: Coincident(g7,g8)
    c: Horizontal(g8)
    c: Coincident(g0,g9)
    c: Horizontal(g9)
    c: Coincident(g10,g8)
    c: Coincident(g10,g9)
    c: Vertical(g9,g-1)
    c: Vertical(g10)
    c: DistanceX(g-1,g1) = 7.5
    c: Vertical(g2)
    c: DistanceY(g8,g-1) = 24
    c: DistanceY(g7,g7) = 9.8
    c: DistanceX(g8,g8) = 4.335
    c: Horizontal(g3)
    c: DistanceX(g-1,g4) = 5.85
    c: DistanceY(g2,g2) = 3
    c: DistanceY(g4,g4) = 8
    c: DistanceX(g5) = 5.5925
    c: DistanceY(g5) = -12.7105
    c: DistanceX(g9,g9) = 3.565
    c: DistanceY(g0,g0) = 12
FEATURE [PartDesign::Revolution] Revolution
  AllowMultiFace = false
  Angle = 360
  Axis = (0,-2e-16,1)
  Base = (0,0,0)
  Placement = pos=(0,0,0) rot=(1,0,0;1.5708rad)
  Profile = -> Sketch041
  ReferenceAxis = -> Sketch041 [V_Axis]
  Reversed = true
FEATURE [Sketcher::SketchObject] Sketch043  label="sk_profileBouchon"
  FullyConstrained = false
  MapMode = 5
  Placement = pos=(0,0,0) rot=(1,0,0;1.5708rad)
  Support = -> [XZ_Plane044]
  expr: Constraints[10] = <<fuse>>.bouchDiamInfCone / 2
  expr: Constraints[11] = <<fuse>>.bouchDiamSupCone / 2
  expr: Constraints[20] = <<fuse>>.bouchHtot
  expr: Constraints[21] = <<fuse>>.bouchDiamFutLaiton / 2
  expr: Constraints[2] = <<fuse>>.bouchHPlastique
  expr: Constraints[4] = <<fuse>>.bouchHLevre
  expr: Constraints[5] = <<fuse>>.bouchDiamLevre / 2
  sketch-geometry (8):
    g0: LineSegment StartX=0 StartY=7.6 StartZ=0 EndX=5.6 EndY=7.6 EndZ=0
    g1: LineSegment StartX=7 StartY=1.26 StartZ=0 EndX=7 EndY=0 EndZ=0
    g2: LineSegment StartX=7 StartY=1.26 StartZ=0 EndX=6.125 EndY=1.26 EndZ=0
    g3: LineSegment StartX=6.125 StartY=1.26 StartZ=0 EndX=5.6 EndY=7.6 EndZ=0
    g4: LineSegment StartX=7 StartY=0 StartZ=0 EndX=4 EndY=0 EndZ=0
    g5: LineSegment StartX=4 StartY=0 StartZ=0 EndX=4 EndY=-4.4 EndZ=0
    g6: LineSegment StartX=4 StartY=-4.4 StartZ=0 EndX=0 EndY=-4.4 EndZ=0
    g7: LineSegment StartX=0 StartY=7.6 StartZ=0 EndX=0 EndY=-4.4 EndZ=0
  constraints (24):
    c: PointOnObject(g0,g-2)
    c: Horizontal(g0)
    c: DistanceY(g-1,g0) = 7.6
    c: Vertical(g1)
    c: DistanceY(g1,g1) = 1.26
    c: DistanceX(g-1,g1) = 7
    c: Coincident(g1,g2)
    c: Coincident(g2,g3)
    c: Coincident(g3,g0)
    c: Horizontal(g2)
    c: DistanceX(g-1,g2) = 6.125
    c: DistanceX(g0,g0) = 5.6
    c: Coincident(g4,g1)
    c: PointOnObject(g4,g-1)
    c: Horizontal(g4)
    c: Coincident(g5,g4)
    c: Vertical(g5)
    c: Coincident(g6,g5)
    c: PointOnObject(g6,g-2)
    c: Horizontal(g6)
    c: DistanceY(g6,g0) = 12
    c: DistanceX(g6,g6) = 4
    c: Coincident(g7,g0)
    c: Coincident(g7,g6)
FEATURE [PartDesign::Revolution] Revolution001
  AllowMultiFace = false
  Angle = 360
  Axis = (0,-2e-16,1)
  Base = (0,0,0)
  Placement = pos=(0,0,0) rot=(1,0,0;1.5708rad)
  Profile = -> Sketch043
  ReferenceAxis = -> Sketch043 [V_Axis]
  Reversed = true
FEATURE [PartDesign::Body] Body011  label="bouchon"
  Group = -> [Sketch043,Revolution001]
  Origin = -> Origin044
  Tip = -> Revolution001
FEATURE [PartDesign::Plane] DatumPlane014  label="planMeplat"
  AttachmentOffset = pos=(0,0,-3) rot=(0,0,1;0rad)
  Length = 60
  MapMode = 2
  Placement = pos=(0,0,-3) rot=(0,0,1;0rad)
  ResizeMode = 0
  Support = -> [XY_Plane042]
  Width = 60
  expr: .AttachmentOffset.Base.z = -<<fuse>>.corpsLevreHauteur
FEATURE [Sketcher::SketchObject] Sketch042  label="sk_meplat"
  FullyConstrained = false
  MapMode = 5
  Placement = pos=(0,0,-3) rot=(0,0,1;0rad)
  Support = -> [DatumPlane014]
  expr: Constraints[10] = <<fuse>>.corpsDiamFilletage
  expr: Constraints[12] = <<fuse>>.corpsLargeurMeplat
  sketch-geometry (5):
    g0: ArcOfCircle CenterX=0 CenterY=0 CenterZ=0 NormalX=0 NormalY=0 NormalZ=1 AngleXU=0 Radius=5.85 StartAngle=3.51353 EndAngle=5.91124
    g1: LineSegment StartX=-5.45 StartY=2.12603 StartZ=0 EndX=-5.45 EndY=-2.12603 EndZ=0
    g2: LineSegment StartX=5.45 StartY=-2.12603 StartZ=0 EndX=5.45 EndY=2.12603 EndZ=0
    g3: ArcOfCircle CenterX=0 CenterY=0 CenterZ=0 NormalX=0 NormalY=0 NormalZ=1 AngleXU=0 Radius=5.85 StartAngle=0.37194 EndAngle=2.76965
    g4: Circle CenterX=0 CenterY=0 CenterZ=0 NormalX=0 NormalY=0 NormalZ=1 AngleXU=0 Radius=10.5
  constraints (15):
    c: Vertical(g1)
    c: Vertical(g2)
    c: Coincident(g0,g1)
    c: Coincident(g3,g1)
    c: Equal(g0,g3)
    c: Coincident(g0,g2)
    c: Coincident(g3,g2)
    c: Coincident(g0,g3)
    c: Coincident(g1,g3)
    c: Coincident(g0,g-1)
    c: Diameter(g3) = 11.7
    c: Symmetric(g1,g2,g-2)
    c: DistanceX(g0,g0) = 10.9
    c: Coincident(g4,g0)
    c: Diameter(g4) = 21
FEATURE [PartDesign::Pocket] Pocket019
  AllowMultiFace = false
  BaseFeature = -> Revolution
  Direction = (1,1,1)
  Length = 13
  Length2 = 100
  Placement = pos=(0,0,0) rot=(1,0,0;1.5708rad)
  Profile = -> Sketch042
  Type = 0
  expr: Length = <<fuse>>.corpsHauteurFilletage + 5
FEATURE [PartDesign::Body] Body010  label="corps002"
  Group = -> [Sketch041,Revolution,Sketch042,DatumPlane014,Pocket019]
  Origin = -> Origin043
  Tip = -> Pocket019
FEATURE [PartDesign::Plane] DatumPlane015  label="planCosse"
  AttachmentOffset = pos=(0,0,1) rot=(0,0,1;0rad)
  Length = 60.4881
  MapMode = 5
  Placement = pos=(1,-2e-16,2e-16) rot=(0.57735,0.57735,0.57735;2.0944rad)
  ResizeMode = 0
  Support = -> [YZ_Plane045]
  Width = 65.4881
FEATURE [Sketcher::SketchObject] Sketch044  label="Sketch003"
  FullyConstrained = true
  MapMode = 5
  Placement = pos=(1,-2e-16,2e-16) rot=(0.57735,0.57735,0.57735;2.0944rad)
  Support = -> [DatumPlane015]
  expr: Constraints[19] = <<fuse>>.corpsHautTot
  sketch-geometry (7):
    g0: LineSegment StartX=0 StartY=-24 StartZ=0 EndX=2 EndY=-24 EndZ=0
    g1: LineSegment StartX=2 StartY=-24 StartZ=0 EndX=2 EndY=-28 EndZ=0
    g2: LineSegment StartX=2 StartY=-28 StartZ=0 EndX=0 EndY=-28 EndZ=0
    g3: LineSegment StartX=0 StartY=-28 StartZ=0 EndX=0 EndY=-24 EndZ=0
    g4: ArcOfCircle CenterX=0 CenterY=-28 CenterZ=0 NormalX=0 NormalY=0 NormalZ=1 AngleXU=0 Radius=2 StartAngle=3.14159 EndAngle=6.28319
    g5: LineSegment StartX=0 StartY=-24 StartZ=0 EndX=-2 EndY=-24 EndZ=0
    g6: LineSegment StartX=-2 StartY=-24 StartZ=0 EndX=-2 EndY=-28 EndZ=0
  constraints (20):
    c: Coincident(g0,g1)
    c: Coincident(g1,g2)
    c: Coincident(g2,g3)
    c: Coincident(g3,g0)
    c: Horizontal(g0)
    c: Horizontal(g2)
    c: Vertical(g1)
    c: Vertical(g3)
    c: Coincident(g4,g2)
    c: Coincident(g4,g1)
    c: Horizontal(g5)
    c: Coincident(g5,g6)
    c: Coincident(g6,g4)
    c: Horizontal(g4,g4)
    c: Vertical(g6)
    c: DistanceX(g0,g0) = 2
    c: Coincident(g5,g0)
    c: DistanceY(g1,g0) = 4
    c: PointOnObject(g0,g-2)
    c: DistanceY(g0,g-1) = 24
FEATURE [PartDesign::Pad] Pad021
  AllowMultiFace = false
  Direction = (1,1,1)
  Length = 0.6
  Length2 = 100
  Placement = pos=(1,0,0) rot=(0.57735,0.57735,0.57735;2.0944rad)
  Profile = -> Sketch044
  Type = 0
FEATURE [Sketcher::SketchObject] Sketch045
  ExternalGeometry = -> [Pad021]
  FullyConstrained = true
  MapMode = 5
  Placement = pos=(1.6,0,1e-16) rot=(0.57735,0.57735,0.57735;2.0944rad)
  Support = -> [Pad021]
  sketch-geometry (1):
    g0: Circle CenterX=0 CenterY=-28 CenterZ=0 NormalX=0 NormalY=0 NormalZ=1 AngleXU=0 Radius=0.875
  constraints (2):
    c: Diameter(g0) = 1.75
    c: Coincident(g0,g-3)
FEATURE [PartDesign::Pocket] Pocket020  label="Pocket001"
  AllowMultiFace = false
  BaseFeature = -> Pad021
  Direction = (1,1,1)
  Length = 5
  Length2 = 100
  Placement = pos=(1,0,0) rot=(0.57735,0.57735,0.57735;2.0944rad)
  Profile = -> Sketch045
  Type = 1
FEATURE [PartDesign::Body] Body012  label="cosse1"
  Group = -> [DatumPlane015,Sketch044,Pad021,Sketch045,Pocket020]
  Origin = -> Origin045
  Placement = pos=(0,0,0) rot=(0,0,1;1.5708rad)
  Tip = -> Pocket020
FEATURE [PartDesign::Plane] DatumPlane016  label="planCosse001"
  AttachmentOffset = pos=(0,0,1) rot=(0,0,1;0rad)
  Length = 60.4873
  MapMode = 5
  Placement = pos=(1,-2e-16,2e-16) rot=(0.57735,0.57735,0.57735;2.0944rad)
  ResizeMode = 0
  Support = -> [YZ_Plane046]
  Width = 65.4787
FEATURE [Sketcher::SketchObject] Sketch046
  FullyConstrained = false
  MapMode = 5
  Placement = pos=(1,-2e-16,2e-16) rot=(0.57735,0.57735,0.57735;2.0944rad)
  Support = -> [DatumPlane016]
  expr: Constraints[19] = <<fuse>>.corpsHautTot
  sketch-geometry (7):
    g0: LineSegment StartX=0 StartY=-24 StartZ=0 EndX=2 EndY=-24 EndZ=0
    g1: LineSegment StartX=2 StartY=-24 StartZ=0 EndX=2 EndY=-28 EndZ=0
    g2: LineSegment StartX=2 StartY=-28 StartZ=0 EndX=0 EndY=-28 EndZ=0
    g3: LineSegment StartX=0 StartY=-28 StartZ=0 EndX=0 EndY=-24 EndZ=0
    g4: ArcOfCircle CenterX=0 CenterY=-28 CenterZ=0 NormalX=0 NormalY=0 NormalZ=1 AngleXU=0 Radius=2 StartAngle=3.14159 EndAngle=6.28319
    g5: LineSegment StartX=0 StartY=-24 StartZ=0 EndX=-2 EndY=-24 EndZ=0
    g6: LineSegment StartX=-2 StartY=-24 StartZ=0 EndX=-2 EndY=-28 EndZ=0
  constraints (20):
    c: Coincident(g0,g1)
    c: Coincident(g1,g2)
    c: Coincident(g2,g3)
    c: Coincident(g3,g0)
    c: Horizontal(g0)
    c: Horizontal(g2)
    c: Vertical(g1)
    c: Vertical(g3)
    c: Coincident(g4,g2)
    c: Coincident(g4,g1)
    c: Horizontal(g5)
    c: Coincident(g5,g6)
    c: Coincident(g6,g4)
    c: Horizontal(g4,g4)
    c: Vertical(g6)
    c: DistanceX(g0,g0) = 2
    c: Coincident(g5,g0)
    c: DistanceY(g1,g0) = 4
    c: PointOnObject(g0,g-2)
    c: DistanceY(g0,g-1) = 24
FEATURE [PartDesign::Pad] Pad022
  AllowMultiFace = false
  Direction = (1,1,1)
  Length = 0.6
  Length2 = 100
  Placement = pos=(1,0,0) rot=(0.57735,0.57735,0.57735;2.0944rad)
  Profile = -> Sketch046
  Type = 0
FEATURE [Sketcher::SketchObject] Sketch047  label="Sketch006"
  ExternalGeometry = -> [Pad022]
  FullyConstrained = false
  MapMode = 5
  Placement = pos=(1.6,0,1e-16) rot=(0.57735,0.57735,0.57735;2.0944rad)
  Support = -> [Pad022]
  sketch-geometry (1):
    g0: Circle CenterX=0 CenterY=-28 CenterZ=0 NormalX=0 NormalY=0 NormalZ=1 AngleXU=0 Radius=0.875
  constraints (2):
    c: Diameter(g0) = 1.75
    c: Coincident(g0,g-3)
FEATURE [PartDesign::Pocket] Pocket021
  AllowMultiFace = false
  BaseFeature = -> Pad022
  Direction = (1,1,1)
  Length = 5
  Length2 = 100
  Placement = pos=(1,0,0) rot=(0.57735,0.57735,0.57735;2.0944rad)
  Profile = -> Sketch047
  Type = 1
FEATURE [PartDesign::Body] Body013  label="cosse002"
  Group = -> [DatumPlane016,Sketch046,Pad022,Sketch047,Pocket021]
  Origin = -> Origin046
  Placement = pos=(-1e-15,-6.2,12) rot=(0,0,1;1.5708rad)
  Tip = -> Pocket021
COMPONENT P16 — recipe-attached ("KTD132UI", modeled in this document).
Construction recipe (the document's own serialized feature program — sketch geometry with constraints, then the solid features built on it; lengths are millimeters unless a unit is written):

FEATURE [Sketcher::SketchObject] Sketch048  label="Sketch"
  FullyConstrained = true
  MapMode = 5
  Support = -> [XY_Plane047]
  expr: Constraints[8] = <<KTD132>>.trouLongeur
  expr: Constraints[9] = <<KTD132>>.trouLargeur
  sketch-geometry (4):
    g0: LineSegment StartX=-42.3 StartY=22.3 StartZ=0 EndX=42.3 EndY=22.3 EndZ=0
    g1: LineSegment StartX=42.3 StartY=22.3 StartZ=0 EndX=42.3 EndY=-22.3 EndZ=0
    g2: LineSegment StartX=42.3 StartY=-22.3 StartZ=0 EndX=-42.3 EndY=-22.3 EndZ=0
    g3: LineSegment StartX=-42.3 StartY=-22.3 StartZ=0 EndX=-42.3 EndY=22.3 EndZ=0
  constraints (10):
    c: Coincident(g0,g1)
    c: Coincident(g1,g2)
    c: Coincident(g2,g3)
    c: Coincident(g3,g0)
    c: Horizontal(g2)
    c: Vertical(g1)
    c: Symmetric(g0,g0,g-2)
    c: Symmetric(g0,g2,g-1)
    c: DistanceX(g0,g0) = 84.6
    c: DistanceY(g1,g1) = 44.6
FEATURE [PartDesign::Pad] Pad023  label="corpsPrincipal"
  AllowMultiFace = false
  Direction = (1,1,1)
  Length = 22.4
  Length2 = 100
  Profile = -> Sketch048
  Reversed = true
  Type = 0
  expr: Length = <<KTD132>>.hauteur - <<KTD132>>.epaisseurRebord
FEATURE [Sketcher::SketchObject] Sketch049
  FullyConstrained = true
  MapMode = 5
  Support = -> [XY_Plane048]
  expr: Constraints[10] = <<KTD132>>.largeur
  expr: Constraints[9] = <<KTD132>>.longueur
  sketch-geometry (4):
    g0: LineSegment StartX=-44.8 StartY=24.8 StartZ=0 EndX=44.8 EndY=24.8 EndZ=0
    g1: LineSegment StartX=44.8 StartY=24.8 StartZ=0 EndX=44.8 EndY=-24.8 EndZ=0
    g2: LineSegment StartX=44.8 StartY=-24.8 StartZ=0 EndX=-44.8 EndY=-24.8 EndZ=0
    g3: LineSegment StartX=-44.8 StartY=-24.8 StartZ=0 EndX=-44.8 EndY=24.8 EndZ=0
  constraints (11):
    c: Coincident(g0,g1)
    c: Coincident(g1,g2)
    c: Coincident(g2,g3)
    c: Coincident(g3,g0)
    c: Horizontal(g0)
    c: Horizontal(g2)
    c: Vertical(g1)
    c: Vertical(g3)
    c: Symmetric(g0,g1,g-1)
    c: DistanceX(g0,g0) = 89.6
    c: DistanceY(g1,g1) = 49.6
FEATURE [PartDesign::Pad] Pad024  label="Pad001"
  AllowMultiFace = false
  BaseFeature = -> Pad023
  Direction = (1,1,1)
  Length = 2
  Length2 = 100
  Profile = -> Sketch049
  Type = 0
  expr: Length = <<KTD132>>.epaisseurRebord
FEATURE [PartDesign::Fillet] Fillet  label="faceAvant001"
  Base = -> Pad024 [Edge16,Edge10,Edge4,Edge7]
  BaseFeature = -> Pad024
  Radius = 0.8
  SupportTransform = false
  UseAllEdges = false
FEATURE [Sketcher::SketchObject] Sketch050  label="Sketch002"
  FullyConstrained = true
  MapMode = 5
  Placement = pos=(0,0,2) rot=(0,0,1;0rad)
  Support = -> [Fillet]
  expr: Constraints[8] = <<KTD132>>.ecranLongueur
  expr: Constraints[9] = <<KTD132>>.ecranLargeur
  sketch-geometry (4):
    g0: LineSegment StartX=-25.5 StartY=15 StartZ=0 EndX=25.5 EndY=15 EndZ=0
    g1: LineSegment StartX=25.5 StartY=15 StartZ=0 EndX=25.5 EndY=-15 EndZ=0
    g2: LineSegment StartX=25.5 StartY=-15 StartZ=0 EndX=-25.5 EndY=-15 EndZ=0
    g3: LineSegment StartX=-25.5 StartY=-15 StartZ=0 EndX=-25.5 EndY=15 EndZ=0
  constraints (11):
    c: Coincident(g0,g1)
    c: Coincident(g1,g2)
    c: Coincident(g2,g3)
    c: Coincident(g3,g0)
    c: Horizontal(g0)
    c: Horizontal(g2)
    c: Vertical(g1)
    c: Vertical(g3)
    c: DistanceX(g0,g0) = 51
    c: DistanceY(g1,g1) = 30
    c: Symmetric(g0,g1,g-1)
FEATURE [PartDesign::Pocket] Pocket023  label="ecran"
  AllowMultiFace = false
  BaseFeature = -> Fillet
  Direction = (1,1,1)
  Length = 2.82
  Length2 = 100
  Profile = -> Sketch050
  Type = 0
  expr: Length = <<KTD132>>.ecranPRof
FEATURE [PartDesign::Chamfer] Chamfer004  label="ecranChamfrein"
  Angle = 45
  Base = -> Pocket023 [Edge27,Edge24,Edge26,Edge25]
  BaseFeature = -> Pocket023
  ChamferType = 0
  FlipDirection = false
  Size = 1.5
  Size2 = 1
  SupportTransform = false
  UseAllEdges = false
FEATURE [Sketcher::SketchObject] Sketch051  label="sk_bouton"
  FullyConstrained = true
  MapMode = 5
  Placement = pos=(0,0,2) rot=(0,0,1;0rad)
  Support = -> [Chamfer004]
  expr: Constraints[1] = <<KTD132>>.boutonPosHorizontale
  expr: Constraints[2] = <<KTD132>>.boutonDiam + <<KTD132>>.boutonJeuDiam
  sketch-geometry (1):
    g0: Circle CenterX=37 CenterY=0 CenterZ=0 NormalX=0 NormalY=0 NormalZ=1 AngleXU=0 Radius=1.81
  constraints (3):
    c: PointOnObject(g0,g-1)
    c: DistanceX(g-1,g0) = 37
    c: Diameter(g0) = 3.62
FEATURE [PartDesign::Pocket] Pocket024  label="boutonTrou"
  AllowMultiFace = false
  BaseFeature = -> Chamfer004
  Direction = (1,1,1)
  Length = 3
  Length2 = 100
  Profile = -> Sketch051
  Type = 0
  expr: Length = <<KTD132>>.boutonHauteur
FEATURE [PartDesign::Plane] DatumPlane017
  AttachmentOffset = pos=(0,0,-22.4) rot=(0,0,1;0rad)
  Length = 102.987
  MapMode = 5
  Placement = pos=(0,0,-22.4) rot=(0,0,1;0rad)
  ResizeMode = 0
  Support = -> [XY_Plane048]
  Width = 63.3866
  expr: .AttachmentOffset.Base.z = -(<<KTD132>>.hauteur - <<KTD132>>.epaisseurRebord)
FEATURE [Sketcher::SketchObject] Sketch052  label="sk_trouConnecteurs"
  FullyConstrained = true
  MapMode = 5
  Placement = pos=(0,0,-22.4) rot=(0,0,1;0rad)
  Support = -> [DatumPlane017]
  expr: Constraints[10] = <<KTD132>>.trouLongeur / 2 - <<KTD132>>.lumiereConnecteurLargeur
  expr: Constraints[7] = <<KTD132>>.lumiereConnecteurLargeur
  expr: Constraints[8] = <<KTD132>>.lumiereConnecteurLongueur
  sketch-geometry (4):
    g0: LineSegment StartX=-42.3 StartY=13 StartZ=0 EndX=-33.3 EndY=13 EndZ=0
    g1: LineSegment StartX=-33.3 StartY=13 StartZ=0 EndX=-33.3 EndY=-13 EndZ=0
    g2: LineSegment StartX=-33.3 StartY=-13 StartZ=0 EndX=-42.3 EndY=-13 EndZ=0
    g3: LineSegment StartX=-42.3 StartY=-13 StartZ=0 EndX=-42.3 EndY=13 EndZ=0
  constraints (11):
    c: Coincident(g0,g1)
    c: Coincident(g1,g2)
    c: Coincident(g2,g3)
    c: Coincident(g3,g0)
    c: Horizontal(g0)
    c: Horizontal(g2)
    c: Vertical(g1)
    c: DistanceX(g0,g0) = 9
    c: DistanceY(g3,g3) = 26
    c: Symmetric(g0,g2,g-1)
    c: DistanceX(g1,g-1) = 33.3
FEATURE [PartDesign::Pocket] Pocket025  label="Pocket002"
  BaseFeature = -> Pocket024
  Direction = (1,1,1)
  Length = 10
  Length2 = 100
  Profile = -> Sketch052
  Reversed = true
  Type = 0
  expr: Length = <<KTD132>>.lumiereConnecteurHauteur
FEATURE [PartDesign::Plane] DatumPlane018  label="planbaseBouton"
  AttachmentOffset = pos=(0,0,-1) rot=(0,0,1;0rad)
  Length = 102.987
  MapMode = 5
  Placement = pos=(0,0,-1) rot=(0,0,1;0rad)
  ResizeMode = 0
  Support = -> [XY_Plane048]
  Width = 63.3866
  expr: .AttachmentOffset.Base.z = -(<<KTD132>>.boutonHauteur - <<KTD132>>.epaisseurRebord)
FEATURE [Sketcher::SketchObject] Sketch007
  FullyConstrained = true
  MapMode = 5
  Placement = pos=(0,0,-1) rot=(0,0,1;0rad)
  Support = -> [DatumPlane018]
  expr: Constraints[1] = <<KTD132>>.boutonPosHorizontale
  expr: Constraints[2] = <<KTD132>>.boutonDiam - <<KTD132>>.boutonJeuDiam
  sketch-geometry (1):
    g0: Circle CenterX=37 CenterY=0 CenterZ=0 NormalX=0 NormalY=0 NormalZ=1 AngleXU=0 Radius=1.51
  constraints (3):
    c: PointOnObject(g0,g-1)
    c: DistanceX(g-1,g0) = 37
    c: Diameter(g0) = 3.02
FEATURE [PartDesign::Pad] Pad002
  BaseFeature = -> Pocket025
  Direction = (1,1,1)
  Length = 3
  Length2 = 100
  Profile = -> Sketch007
  Type = 0
  expr: Length = <<KTD132>>.boutonHauteur
FEATURE [PartDesign::Body] Body014  label="Body"
  Group = -> [Sketch048,Pad023,Sketch049,Pad024,Fillet,Sketch050,Pocket023,Chamfer004,Sketch051,Pocket024,DatumPlane017,Sketch052,Pocket025,DatumPlane018,Sketch007,Pad002]
  Origin = -> Origin048
  Tip = -> Pad002
COMPONENT P17 — geometry summary ("switch"; no construction recipe available for this part):
  bounding box: 38.3 x 33.1 x 13.9 mm
  tessellated surface: 4,456 triangles
  volume: 6127 mm^3 (35% of its bounding box)
PROVENANCE & LICENSES
A FreeCAD (.FCStd) document from a public repository crawl; recipes are the document's own serialized feature recipes (and, for linked parts, companion documents' recipes).
License: as declared in the source repository (recorded in the dataset sidecar).
